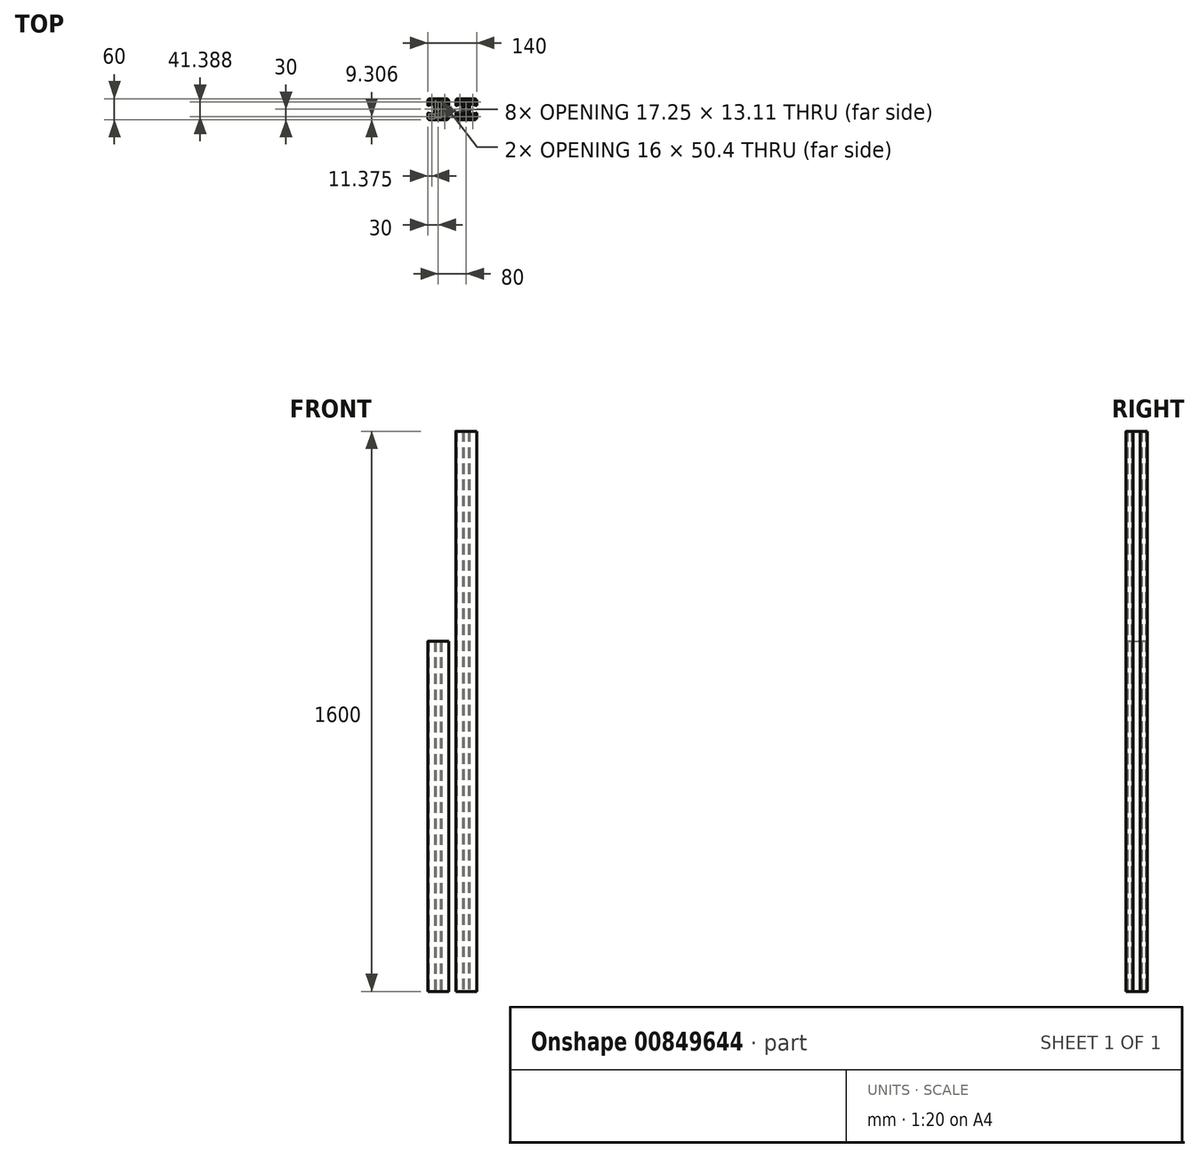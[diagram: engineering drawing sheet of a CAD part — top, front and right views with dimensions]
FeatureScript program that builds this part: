
annotation { "Feature Type Name" : "Feature", "Feature Type Description" : "" }
export const myFeature = defineFeature(function(context is Context, id is Id, definition is map)
    precondition{}
    {
        {
            var Q0;
            Q0=qCreatedBy(makeId("Top.planeOp"),FACE);
            var sketch = newSketch(context, id + "F0", { "sketchPlane" : qUnion([Q0])});
            skLineSegment(sketch, "E0", {"start": v(-5.2, -25.2) * mm, "end": v(5.2, -25.2) * mm});
            skLineSegment(sketch, "E1", {"start": v(6.2, -24.2) * mm, "end": v(6.2, -5.4) * mm});
            skLineSegment(sketch, "E2", {"start": v(6.2, 5.4) * mm, "end": v(6.2, 24.2) * mm});
            skLineSegment(sketch, "E3", {"start": v(5.2, 25.2) * mm, "end": v(-5.2, 25.2) * mm});
            skLineSegment(sketch, "E4", {"start": v(-6.2, 24.2) * mm, "end": v(-6.2, 5.4) * mm});
            skLineSegment(sketch, "E5", {"start": v(-6.2, -5.4) * mm, "end": v(-6.2, -24.2) * mm});
            skLineSegment(sketch, "E6", {"start": v(-24, -27.25) * mm, "end": v(-11, -27.25) * mm});
            skLineSegment(sketch, "E7", {"start": v(-10, -26.25) * mm, "end": v(-10, -19.22) * mm});
            skLineSegment(sketch, "E8", {"start": v(-10.74, -18.26) * mm, "end": v(-26, -14.17) * mm});
            skLineSegment(sketch, "E9", {"start": v(-27.25, -15.14) * mm, "end": v(-27.25, -24) * mm});
            skLineSegment(sketch, "E10", {"start": v(-26, 14.17) * mm, "end": v(-10.74, 18.26) * mm});
            skLineSegment(sketch, "E11", {"start": v(-10, 19.22) * mm, "end": v(-10, 26.25) * mm});
            skLineSegment(sketch, "E12", {"start": v(-11, 27.25) * mm, "end": v(-24, 27.25) * mm});
            skLineSegment(sketch, "E13", {"start": v(-27.25, 24) * mm, "end": v(-27.25, 15.14) * mm});
            skLineSegment(sketch, "E14", {"start": v(10, -14.3) * mm, "end": v(10, 14.3) * mm});
            skLineSegment(sketch, "E15", {"start": v(28.43, -10.67) * mm, "end": v(11.26, -15.27) * mm});
            skLineSegment(sketch, "E16", {"start": v(30, -24) * mm, "end": v(30, -11.88) * mm});
            skLineSegment(sketch, "E17", {"start": v(-24, -30) * mm, "end": v(24, -30) * mm});
            skLineSegment(sketch, "E18", {"start": v(-30, -11.88) * mm, "end": v(-30, -24) * mm});
            skLineSegment(sketch, "E19", {"start": v(-11.26, -15.27) * mm, "end": v(-28.43, -10.67) * mm});
            skLineSegment(sketch, "E20", {"start": v(-10, 14.3) * mm, "end": v(-10, -14.3) * mm});
            skLineSegment(sketch, "E21", {"start": v(-28.43, 10.67) * mm, "end": v(-11.26, 15.27) * mm});
            skLineSegment(sketch, "E22", {"start": v(-30, 24) * mm, "end": v(-30, 11.88) * mm});
            skLineSegment(sketch, "E23", {"start": v(24, 30) * mm, "end": v(-24, 30) * mm});
            skLineSegment(sketch, "E24", {"start": v(30, 11.88) * mm, "end": v(30, 24) * mm});
            skLineSegment(sketch, "E25", {"start": v(11.26, 15.27) * mm, "end": v(28.43, 10.67) * mm});
            skLineSegment(sketch, "E26", {"start": v(26, -14.17) * mm, "end": v(10.74, -18.26) * mm});
            skLineSegment(sketch, "E27", {"start": v(10, -19.22) * mm, "end": v(10, -26.25) * mm});
            skLineSegment(sketch, "E28", {"start": v(11, -27.25) * mm, "end": v(24, -27.25) * mm});
            skLineSegment(sketch, "E29", {"start": v(27.25, -24) * mm, "end": v(27.25, -15.14) * mm});
            skLineSegment(sketch, "E30", {"start": v(24, 27.25) * mm, "end": v(11, 27.25) * mm});
            skLineSegment(sketch, "E31", {"start": v(10, 26.25) * mm, "end": v(10, 19.22) * mm});
            skLineSegment(sketch, "E32", {"start": v(10.74, 18.26) * mm, "end": v(26, 14.17) * mm});
            skLineSegment(sketch, "E33", {"start": v(27.25, 15.14) * mm, "end": v(27.25, 24) * mm});
            skArc(sketch, "E34", {"start": v(-6.2, -24.2) * mm, "mid": v(-5.9, -24.9) * mm, "end": v(-5.2, -25.2) * mm});
            skArc(sketch, "E35", {"start": v(5.2, -25.2) * mm, "mid": v(5.9, -24.9) * mm, "end": v(6.2, -24.2) * mm});
            skArc(sketch, "E36", {"start": v(6.4, -4.8) * mm, "mid": v(6.25, -5.08) * mm, "end": v(6.2, -5.4) * mm});
            skArc(sketch, "E37", {"start": v(6.4, -4.8) * mm, "mid": v(8, 0) * mm, "end": v(6.4, 4.8) * mm});
            skArc(sketch, "E38", {"start": v(6.2, 5.4) * mm, "mid": v(6.25, 5.08) * mm, "end": v(6.4, 4.8) * mm});
            skArc(sketch, "E39", {"start": v(6.2, 24.2) * mm, "mid": v(5.9, 24.9) * mm, "end": v(5.2, 25.2) * mm});
            skArc(sketch, "E40", {"start": v(-5.2, 25.2) * mm, "mid": v(-5.9, 24.9) * mm, "end": v(-6.2, 24.2) * mm});
            skArc(sketch, "E41", {"start": v(-6.4, 4.8) * mm, "mid": v(-6.25, 5.08) * mm, "end": v(-6.2, 5.4) * mm});
            skArc(sketch, "E42", {"start": v(-6.4, 4.8) * mm, "mid": v(-8, 0) * mm, "end": v(-6.4, -4.8) * mm});
            skArc(sketch, "E43", {"start": v(-6.2, -5.4) * mm, "mid": v(-6.25, -5.08) * mm, "end": v(-6.4, -4.8) * mm});
            skArc(sketch, "E44", {"start": v(-27.25, -24) * mm, "mid": v(-26.3, -26.3) * mm, "end": v(-24, -27.25) * mm});
            skArc(sketch, "E45", {"start": v(-11, -27.25) * mm, "mid": v(-10.3, -26.96) * mm, "end": v(-10, -26.25) * mm});
            skArc(sketch, "E46", {"start": v(-10, -19.22) * mm, "mid": v(-10.2, -18.61) * mm, "end": v(-10.74, -18.26) * mm});
            skArc(sketch, "E47", {"start": v(-26, -14.17) * mm, "mid": v(-26.86, -14.34) * mm, "end": v(-27.25, -15.14) * mm});
            skArc(sketch, "E48", {"start": v(-27.25, 15.14) * mm, "mid": v(-26.86, 14.34) * mm, "end": v(-26, 14.17) * mm});
            skArc(sketch, "E49", {"start": v(-10.74, 18.26) * mm, "mid": v(-10.2, 18.61) * mm, "end": v(-10, 19.22) * mm});
            skArc(sketch, "E50", {"start": v(-10, 26.25) * mm, "mid": v(-10.3, 26.96) * mm, "end": v(-11, 27.25) * mm});
            skArc(sketch, "E51", {"start": v(-24, 27.25) * mm, "mid": v(-26.3, 26.3) * mm, "end": v(-27.25, 24) * mm});
            skArc(sketch, "E52", {"start": v(11.26, 15.27) * mm, "mid": v(10.4, 15.1) * mm, "end": v(10, 14.3) * mm});
            skArc(sketch, "E53", {"start": v(10, -14.3) * mm, "mid": v(10.4, -15.1) * mm, "end": v(11.26, -15.27) * mm});
            skArc(sketch, "E54", {"start": v(30, -11.88) * mm, "mid": v(29.51, -10.89) * mm, "end": v(28.43, -10.67) * mm});
            skArc(sketch, "E55", {"start": v(24, -30) * mm, "mid": v(28.24, -28.24) * mm, "end": v(30, -24) * mm});
            skArc(sketch, "E56", {"start": v(-30, -24) * mm, "mid": v(-28.24, -28.24) * mm, "end": v(-24, -30) * mm});
            skArc(sketch, "E57", {"start": v(-28.43, -10.67) * mm, "mid": v(-29.51, -10.89) * mm, "end": v(-30, -11.88) * mm});
            skArc(sketch, "E58", {"start": v(-11.26, -15.27) * mm, "mid": v(-10.4, -15.1) * mm, "end": v(-10, -14.3) * mm});
            skArc(sketch, "E59", {"start": v(-10, 14.3) * mm, "mid": v(-10.4, 15.1) * mm, "end": v(-11.26, 15.27) * mm});
            skArc(sketch, "E60", {"start": v(-30, 11.88) * mm, "mid": v(-29.51, 10.89) * mm, "end": v(-28.43, 10.67) * mm});
            skArc(sketch, "E61", {"start": v(-24, 30) * mm, "mid": v(-28.24, 28.24) * mm, "end": v(-30, 24) * mm});
            skArc(sketch, "E62", {"start": v(30, 24) * mm, "mid": v(28.24, 28.24) * mm, "end": v(24, 30) * mm});
            skArc(sketch, "E63", {"start": v(28.43, 10.67) * mm, "mid": v(29.51, 10.89) * mm, "end": v(30, 11.88) * mm});
            skArc(sketch, "E64", {"start": v(27.25, -15.14) * mm, "mid": v(26.86, -14.34) * mm, "end": v(26, -14.17) * mm});
            skArc(sketch, "E65", {"start": v(10.74, -18.26) * mm, "mid": v(10.2, -18.61) * mm, "end": v(10, -19.22) * mm});
            skArc(sketch, "E66", {"start": v(10, -26.25) * mm, "mid": v(10.3, -26.96) * mm, "end": v(11, -27.25) * mm});
            skArc(sketch, "E67", {"start": v(24, -27.25) * mm, "mid": v(26.3, -26.3) * mm, "end": v(27.25, -24) * mm});
            skArc(sketch, "E68", {"start": v(11, 27.25) * mm, "mid": v(10.3, 26.96) * mm, "end": v(10, 26.25) * mm});
            skArc(sketch, "E69", {"start": v(10, 19.22) * mm, "mid": v(10.2, 18.61) * mm, "end": v(10.74, 18.26) * mm});
            skArc(sketch, "E70", {"start": v(26, 14.17) * mm, "mid": v(26.86, 14.34) * mm, "end": v(27.25, 15.14) * mm});
            skArc(sketch, "E71", {"start": v(27.25, 24) * mm, "mid": v(26.3, 26.3) * mm, "end": v(24, 27.25) * mm});
            skLineSegment(sketch, "E72.1.0.0", {"start": v(90.74, 18.26) * mm, "end": v(106, 14.17) * mm});
            skLineSegment(sketch, "E72.1.0.1", {"start": v(56, -30) * mm, "end": v(104, -30) * mm});
            skLineSegment(sketch, "E72.1.0.2", {"start": v(108.43, -10.67) * mm, "end": v(91.26, -15.27) * mm});
            skLineSegment(sketch, "E72.1.0.3", {"start": v(107.25, 15.14) * mm, "end": v(107.25, 24) * mm});
            skLineSegment(sketch, "E72.1.0.4", {"start": v(86.2, 5.4) * mm, "end": v(86.2, 24.2) * mm});
            skLineSegment(sketch, "E72.1.0.5", {"start": v(91, -27.25) * mm, "end": v(104, -27.25) * mm});
            skLineSegment(sketch, "E72.1.0.6", {"start": v(86.2, -24.2) * mm, "end": v(86.2, -5.4) * mm});
            skLineSegment(sketch, "E72.1.0.7", {"start": v(51.57, 10.67) * mm, "end": v(68.74, 15.27) * mm});
            skLineSegment(sketch, "E72.1.0.8", {"start": v(50, -11.88) * mm, "end": v(50, -24) * mm});
            skLineSegment(sketch, "E72.1.0.9", {"start": v(74.8, -25.2) * mm, "end": v(85.2, -25.2) * mm});
            skLineSegment(sketch, "E72.1.0.10", {"start": v(70, 14.3) * mm, "end": v(70, -14.3) * mm});
            skLineSegment(sketch, "E72.1.0.11", {"start": v(90, -14.3) * mm, "end": v(90, 14.3) * mm});
            skLineSegment(sketch, "E72.1.0.12", {"start": v(73.8, -5.4) * mm, "end": v(73.8, -24.2) * mm});
            skArc(sketch, "E72.1.0.13", {"start": v(56, 30) * mm, "mid": v(51.76, 28.24) * mm, "end": v(50, 24) * mm});
            skLineSegment(sketch, "E72.1.0.14", {"start": v(69.26, -18.26) * mm, "end": v(54, -14.17) * mm});
            skArc(sketch, "E72.1.0.15", {"start": v(110, 24) * mm, "mid": v(108.24, 28.24) * mm, "end": v(104, 30) * mm});
            skArc(sketch, "E72.1.0.16", {"start": v(104, -30) * mm, "mid": v(108.24, -28.24) * mm, "end": v(110, -24) * mm});
            skLineSegment(sketch, "E72.1.0.17", {"start": v(73.8, 24.2) * mm, "end": v(73.8, 5.4) * mm});
            skLineSegment(sketch, "E72.1.0.18", {"start": v(104, 30) * mm, "end": v(56, 30) * mm});
            skLineSegment(sketch, "E72.1.0.19", {"start": v(56, -27.25) * mm, "end": v(69, -27.25) * mm});
            skLineSegment(sketch, "E72.1.0.20", {"start": v(54, 14.17) * mm, "end": v(69.26, 18.26) * mm});
            skLineSegment(sketch, "E72.1.0.21", {"start": v(50, 24) * mm, "end": v(50, 11.88) * mm});
            skLineSegment(sketch, "E72.1.0.22", {"start": v(85.2, 25.2) * mm, "end": v(74.8, 25.2) * mm});
            skLineSegment(sketch, "E72.1.0.23", {"start": v(91.26, 15.27) * mm, "end": v(108.43, 10.67) * mm});
            skLineSegment(sketch, "E72.1.0.24", {"start": v(52.75, 24) * mm, "end": v(52.75, 15.14) * mm});
            skLineSegment(sketch, "E72.1.0.25", {"start": v(107.25, -24) * mm, "end": v(107.25, -15.14) * mm});
            skArc(sketch, "E72.1.0.26", {"start": v(73.6, 4.8) * mm, "mid": v(72, 0) * mm, "end": v(73.6, -4.8) * mm});
            skLineSegment(sketch, "E72.1.0.27", {"start": v(52.75, -15.14) * mm, "end": v(52.75, -24) * mm});
            skLineSegment(sketch, "E72.1.0.28", {"start": v(106, -14.17) * mm, "end": v(90.74, -18.26) * mm});
            skLineSegment(sketch, "E72.1.0.29", {"start": v(68.74, -15.27) * mm, "end": v(51.57, -10.67) * mm});
            skLineSegment(sketch, "E72.1.0.30", {"start": v(110, 11.88) * mm, "end": v(110, 24) * mm});
            skLineSegment(sketch, "E72.1.0.31", {"start": v(104, 27.25) * mm, "end": v(91, 27.25) * mm});
            skArc(sketch, "E72.1.0.32", {"start": v(86.4, -4.8) * mm, "mid": v(88, 0) * mm, "end": v(86.4, 4.8) * mm});
            skArc(sketch, "E72.1.0.33", {"start": v(50, -24) * mm, "mid": v(51.76, -28.24) * mm, "end": v(56, -30) * mm});
            skLineSegment(sketch, "E72.1.0.34", {"start": v(110, -24) * mm, "end": v(110, -11.88) * mm});
            skLineSegment(sketch, "E72.1.0.35", {"start": v(69, 27.25) * mm, "end": v(56, 27.25) * mm});
            skArc(sketch, "E72.1.0.36", {"start": v(85.2, -25.2) * mm, "mid": v(85.9, -24.9) * mm, "end": v(86.2, -24.2) * mm});
            skArc(sketch, "E72.1.0.37", {"start": v(52.75, -24) * mm, "mid": v(53.7, -26.3) * mm, "end": v(56, -27.25) * mm});
            skArc(sketch, "E72.1.0.38", {"start": v(107.25, -15.14) * mm, "mid": v(106.86, -14.34) * mm, "end": v(106, -14.17) * mm});
            skArc(sketch, "E72.1.0.39", {"start": v(90, -26.25) * mm, "mid": v(90.3, -26.96) * mm, "end": v(91, -27.25) * mm});
            skArc(sketch, "E72.1.0.40", {"start": v(86.2, 5.4) * mm, "mid": v(86.25, 5.08) * mm, "end": v(86.4, 4.8) * mm});
            skArc(sketch, "E72.1.0.41", {"start": v(104, -27.25) * mm, "mid": v(106.3, -26.3) * mm, "end": v(107.25, -24) * mm});
            skArc(sketch, "E72.1.0.42", {"start": v(73.6, 4.8) * mm, "mid": v(73.75, 5.08) * mm, "end": v(73.8, 5.4) * mm});
            skLineSegment(sketch, "E72.1.0.43", {"start": v(90, 26.25) * mm, "end": v(90, 19.22) * mm});
            skArc(sketch, "E72.1.0.44", {"start": v(110, -11.88) * mm, "mid": v(109.51, -10.89) * mm, "end": v(108.43, -10.67) * mm});
            skArc(sketch, "E72.1.0.45", {"start": v(90, -14.3) * mm, "mid": v(90.4, -15.1) * mm, "end": v(91.26, -15.27) * mm});
            skArc(sketch, "E72.1.0.46", {"start": v(91, 27.25) * mm, "mid": v(90.3, 26.96) * mm, "end": v(90, 26.25) * mm});
            skArc(sketch, "E72.1.0.47", {"start": v(56, 27.25) * mm, "mid": v(53.7, 26.3) * mm, "end": v(52.75, 24) * mm});
            skArc(sketch, "E72.1.0.48", {"start": v(106, 14.17) * mm, "mid": v(106.86, 14.34) * mm, "end": v(107.25, 15.14) * mm});
            skArc(sketch, "E72.1.0.49", {"start": v(108.43, 10.67) * mm, "mid": v(109.51, 10.89) * mm, "end": v(110, 11.88) * mm});
            skArc(sketch, "E72.1.0.50", {"start": v(90, 19.22) * mm, "mid": v(90.2, 18.61) * mm, "end": v(90.74, 18.26) * mm});
            skArc(sketch, "E72.1.0.51", {"start": v(91.26, 15.27) * mm, "mid": v(90.4, 15.1) * mm, "end": v(90, 14.3) * mm});
            skArc(sketch, "E72.1.0.52", {"start": v(107.25, 24) * mm, "mid": v(106.3, 26.3) * mm, "end": v(104, 27.25) * mm});
            skArc(sketch, "E72.1.0.53", {"start": v(51.57, -10.67) * mm, "mid": v(50.49, -10.89) * mm, "end": v(50, -11.88) * mm});
            skLineSegment(sketch, "E72.1.0.54", {"start": v(90, -19.22) * mm, "end": v(90, -26.25) * mm});
            skArc(sketch, "E72.1.0.55", {"start": v(73.8, -24.2) * mm, "mid": v(74.1, -24.9) * mm, "end": v(74.8, -25.2) * mm});
            skArc(sketch, "E72.1.0.56", {"start": v(90.74, -18.26) * mm, "mid": v(90.2, -18.61) * mm, "end": v(90, -19.22) * mm});
            skArc(sketch, "E72.1.0.57", {"start": v(54, -14.17) * mm, "mid": v(53.14, -14.34) * mm, "end": v(52.75, -15.14) * mm});
            skArc(sketch, "E72.1.0.58", {"start": v(50, 11.88) * mm, "mid": v(50.49, 10.89) * mm, "end": v(51.57, 10.67) * mm});
            skLineSegment(sketch, "E72.1.0.59", {"start": v(70, -26.25) * mm, "end": v(70, -19.22) * mm});
            skArc(sketch, "E72.1.0.60", {"start": v(69.26, 18.26) * mm, "mid": v(69.8, 18.61) * mm, "end": v(70, 19.22) * mm});
            skArc(sketch, "E72.1.0.61", {"start": v(86.2, 24.2) * mm, "mid": v(85.9, 24.9) * mm, "end": v(85.2, 25.2) * mm});
            skArc(sketch, "E72.1.0.62", {"start": v(52.75, 15.14) * mm, "mid": v(53.14, 14.34) * mm, "end": v(54, 14.17) * mm});
            skArc(sketch, "E72.1.0.63", {"start": v(70, -19.22) * mm, "mid": v(69.8, -18.61) * mm, "end": v(69.26, -18.26) * mm});
            skArc(sketch, "E72.1.0.64", {"start": v(74.8, 25.2) * mm, "mid": v(74.1, 24.9) * mm, "end": v(73.8, 24.2) * mm});
            skArc(sketch, "E72.1.0.65", {"start": v(70, 26.25) * mm, "mid": v(69.7, 26.96) * mm, "end": v(69, 27.25) * mm});
            skArc(sketch, "E72.1.0.66", {"start": v(70, 14.3) * mm, "mid": v(69.6, 15.1) * mm, "end": v(68.74, 15.27) * mm});
            skLineSegment(sketch, "E72.1.0.67", {"start": v(70, 19.22) * mm, "end": v(70, 26.25) * mm});
            skArc(sketch, "E72.1.0.68", {"start": v(68.74, -15.27) * mm, "mid": v(69.6, -15.1) * mm, "end": v(70, -14.3) * mm});
            skArc(sketch, "E72.1.0.69", {"start": v(69, -27.25) * mm, "mid": v(69.7, -26.96) * mm, "end": v(70, -26.25) * mm});
            skArc(sketch, "E72.1.0.70", {"start": v(86.4, -4.8) * mm, "mid": v(86.25, -5.08) * mm, "end": v(86.2, -5.4) * mm});
            skArc(sketch, "E72.1.0.71", {"start": v(73.8, -5.4) * mm, "mid": v(73.75, -5.08) * mm, "end": v(73.6, -4.8) * mm});
            skLineSegment(sketch, "E72.2.0.0", {"start": v(170.74, 18.26) * mm, "end": v(186, 14.17) * mm});
            skLineSegment(sketch, "E72.2.0.1", {"start": v(136, -30) * mm, "end": v(184, -30) * mm});
            skLineSegment(sketch, "E72.2.0.2", {"start": v(188.43, -10.67) * mm, "end": v(171.26, -15.27) * mm});
            skLineSegment(sketch, "E72.2.0.3", {"start": v(187.25, 15.14) * mm, "end": v(187.25, 24) * mm});
            skLineSegment(sketch, "E72.2.0.4", {"start": v(166.2, 5.4) * mm, "end": v(166.2, 24.2) * mm});
            skLineSegment(sketch, "E72.2.0.5", {"start": v(171, -27.25) * mm, "end": v(184, -27.25) * mm});
            skLineSegment(sketch, "E72.2.0.6", {"start": v(166.2, -24.2) * mm, "end": v(166.2, -5.4) * mm});
            skLineSegment(sketch, "E72.2.0.7", {"start": v(131.57, 10.67) * mm, "end": v(148.74, 15.27) * mm});
            skLineSegment(sketch, "E72.2.0.8", {"start": v(130, -11.88) * mm, "end": v(130, -24) * mm});
            skLineSegment(sketch, "E72.2.0.9", {"start": v(154.8, -25.2) * mm, "end": v(165.2, -25.2) * mm});
            skLineSegment(sketch, "E72.2.0.10", {"start": v(150, 14.3) * mm, "end": v(150, -14.3) * mm});
            skLineSegment(sketch, "E72.2.0.11", {"start": v(170, -14.3) * mm, "end": v(170, 14.3) * mm});
            skLineSegment(sketch, "E72.2.0.12", {"start": v(153.8, -5.4) * mm, "end": v(153.8, -24.2) * mm});
            skArc(sketch, "E72.2.0.13", {"start": v(136, 30) * mm, "mid": v(131.76, 28.24) * mm, "end": v(130, 24) * mm});
            skLineSegment(sketch, "E72.2.0.14", {"start": v(149.26, -18.26) * mm, "end": v(134, -14.17) * mm});
            skArc(sketch, "E72.2.0.15", {"start": v(190, 24) * mm, "mid": v(188.24, 28.24) * mm, "end": v(184, 30) * mm});
            skArc(sketch, "E72.2.0.16", {"start": v(184, -30) * mm, "mid": v(188.24, -28.24) * mm, "end": v(190, -24) * mm});
            skLineSegment(sketch, "E72.2.0.17", {"start": v(153.8, 24.2) * mm, "end": v(153.8, 5.4) * mm});
            skLineSegment(sketch, "E72.2.0.18", {"start": v(184, 30) * mm, "end": v(136, 30) * mm});
            skLineSegment(sketch, "E72.2.0.19", {"start": v(136, -27.25) * mm, "end": v(149, -27.25) * mm});
            skLineSegment(sketch, "E72.2.0.20", {"start": v(134, 14.17) * mm, "end": v(149.26, 18.26) * mm});
            skLineSegment(sketch, "E72.2.0.21", {"start": v(130, 24) * mm, "end": v(130, 11.88) * mm});
            skLineSegment(sketch, "E72.2.0.22", {"start": v(165.2, 25.2) * mm, "end": v(154.8, 25.2) * mm});
            skLineSegment(sketch, "E72.2.0.23", {"start": v(171.26, 15.27) * mm, "end": v(188.43, 10.67) * mm});
            skLineSegment(sketch, "E72.2.0.24", {"start": v(132.75, 24) * mm, "end": v(132.75, 15.14) * mm});
            skLineSegment(sketch, "E72.2.0.25", {"start": v(187.25, -24) * mm, "end": v(187.25, -15.14) * mm});
            skArc(sketch, "E72.2.0.26", {"start": v(153.6, 4.8) * mm, "mid": v(152, 0) * mm, "end": v(153.6, -4.8) * mm});
            skLineSegment(sketch, "E72.2.0.27", {"start": v(132.75, -15.14) * mm, "end": v(132.75, -24) * mm});
            skLineSegment(sketch, "E72.2.0.28", {"start": v(186, -14.17) * mm, "end": v(170.74, -18.26) * mm});
            skLineSegment(sketch, "E72.2.0.29", {"start": v(148.74, -15.27) * mm, "end": v(131.57, -10.67) * mm});
            skLineSegment(sketch, "E72.2.0.30", {"start": v(190, 11.88) * mm, "end": v(190, 24) * mm});
            skLineSegment(sketch, "E72.2.0.31", {"start": v(184, 27.25) * mm, "end": v(171, 27.25) * mm});
            skArc(sketch, "E72.2.0.32", {"start": v(166.4, -4.8) * mm, "mid": v(168, 0) * mm, "end": v(166.4, 4.8) * mm});
            skArc(sketch, "E72.2.0.33", {"start": v(130, -24) * mm, "mid": v(131.76, -28.24) * mm, "end": v(136, -30) * mm});
            skLineSegment(sketch, "E72.2.0.34", {"start": v(190, -24) * mm, "end": v(190, -11.88) * mm});
            skLineSegment(sketch, "E72.2.0.35", {"start": v(149, 27.25) * mm, "end": v(136, 27.25) * mm});
            skArc(sketch, "E72.2.0.36", {"start": v(165.2, -25.2) * mm, "mid": v(165.9, -24.9) * mm, "end": v(166.2, -24.2) * mm});
            skArc(sketch, "E72.2.0.37", {"start": v(132.75, -24) * mm, "mid": v(133.7, -26.3) * mm, "end": v(136, -27.25) * mm});
            skArc(sketch, "E72.2.0.38", {"start": v(187.25, -15.14) * mm, "mid": v(186.86, -14.34) * mm, "end": v(186, -14.17) * mm});
            skArc(sketch, "E72.2.0.39", {"start": v(170, -26.25) * mm, "mid": v(170.3, -26.96) * mm, "end": v(171, -27.25) * mm});
            skArc(sketch, "E72.2.0.40", {"start": v(166.2, 5.4) * mm, "mid": v(166.25, 5.08) * mm, "end": v(166.4, 4.8) * mm});
            skArc(sketch, "E72.2.0.41", {"start": v(184, -27.25) * mm, "mid": v(186.3, -26.3) * mm, "end": v(187.25, -24) * mm});
            skArc(sketch, "E72.2.0.42", {"start": v(153.6, 4.8) * mm, "mid": v(153.75, 5.08) * mm, "end": v(153.8, 5.4) * mm});
            skLineSegment(sketch, "E72.2.0.43", {"start": v(170, 26.25) * mm, "end": v(170, 19.22) * mm});
            skArc(sketch, "E72.2.0.44", {"start": v(190, -11.88) * mm, "mid": v(189.51, -10.89) * mm, "end": v(188.43, -10.67) * mm});
            skArc(sketch, "E72.2.0.45", {"start": v(170, -14.3) * mm, "mid": v(170.4, -15.1) * mm, "end": v(171.26, -15.27) * mm});
            skArc(sketch, "E72.2.0.46", {"start": v(171, 27.25) * mm, "mid": v(170.3, 26.96) * mm, "end": v(170, 26.25) * mm});
            skArc(sketch, "E72.2.0.47", {"start": v(136, 27.25) * mm, "mid": v(133.7, 26.3) * mm, "end": v(132.75, 24) * mm});
            skArc(sketch, "E72.2.0.48", {"start": v(186, 14.17) * mm, "mid": v(186.86, 14.34) * mm, "end": v(187.25, 15.14) * mm});
            skArc(sketch, "E72.2.0.49", {"start": v(188.43, 10.67) * mm, "mid": v(189.51, 10.89) * mm, "end": v(190, 11.88) * mm});
            skArc(sketch, "E72.2.0.50", {"start": v(170, 19.22) * mm, "mid": v(170.2, 18.61) * mm, "end": v(170.74, 18.26) * mm});
            skArc(sketch, "E72.2.0.51", {"start": v(171.26, 15.27) * mm, "mid": v(170.4, 15.1) * mm, "end": v(170, 14.3) * mm});
            skArc(sketch, "E72.2.0.52", {"start": v(187.25, 24) * mm, "mid": v(186.3, 26.3) * mm, "end": v(184, 27.25) * mm});
            skArc(sketch, "E72.2.0.53", {"start": v(131.57, -10.67) * mm, "mid": v(130.49, -10.89) * mm, "end": v(130, -11.88) * mm});
            skLineSegment(sketch, "E72.2.0.54", {"start": v(170, -19.22) * mm, "end": v(170, -26.25) * mm});
            skArc(sketch, "E72.2.0.55", {"start": v(153.8, -24.2) * mm, "mid": v(154.1, -24.9) * mm, "end": v(154.8, -25.2) * mm});
            skArc(sketch, "E72.2.0.56", {"start": v(170.74, -18.26) * mm, "mid": v(170.2, -18.61) * mm, "end": v(170, -19.22) * mm});
            skArc(sketch, "E72.2.0.57", {"start": v(134, -14.17) * mm, "mid": v(133.14, -14.34) * mm, "end": v(132.75, -15.14) * mm});
            skArc(sketch, "E72.2.0.58", {"start": v(130, 11.88) * mm, "mid": v(130.49, 10.89) * mm, "end": v(131.57, 10.67) * mm});
            skLineSegment(sketch, "E72.2.0.59", {"start": v(150, -26.25) * mm, "end": v(150, -19.22) * mm});
            skArc(sketch, "E72.2.0.60", {"start": v(149.26, 18.26) * mm, "mid": v(149.8, 18.61) * mm, "end": v(150, 19.22) * mm});
            skArc(sketch, "E72.2.0.61", {"start": v(166.2, 24.2) * mm, "mid": v(165.9, 24.9) * mm, "end": v(165.2, 25.2) * mm});
            skArc(sketch, "E72.2.0.62", {"start": v(132.75, 15.14) * mm, "mid": v(133.14, 14.34) * mm, "end": v(134, 14.17) * mm});
            skArc(sketch, "E72.2.0.63", {"start": v(150, -19.22) * mm, "mid": v(149.8, -18.61) * mm, "end": v(149.26, -18.26) * mm});
            skArc(sketch, "E72.2.0.64", {"start": v(154.8, 25.2) * mm, "mid": v(154.1, 24.9) * mm, "end": v(153.8, 24.2) * mm});
            skArc(sketch, "E72.2.0.65", {"start": v(150, 26.25) * mm, "mid": v(149.7, 26.96) * mm, "end": v(149, 27.25) * mm});
            skArc(sketch, "E72.2.0.66", {"start": v(150, 14.3) * mm, "mid": v(149.6, 15.1) * mm, "end": v(148.74, 15.27) * mm});
            skLineSegment(sketch, "E72.2.0.67", {"start": v(150, 19.22) * mm, "end": v(150, 26.25) * mm});
            skArc(sketch, "E72.2.0.68", {"start": v(148.74, -15.27) * mm, "mid": v(149.6, -15.1) * mm, "end": v(150, -14.3) * mm});
            skArc(sketch, "E72.2.0.69", {"start": v(149, -27.25) * mm, "mid": v(149.7, -26.96) * mm, "end": v(150, -26.25) * mm});
            skArc(sketch, "E72.2.0.70", {"start": v(166.4, -4.8) * mm, "mid": v(166.25, -5.08) * mm, "end": v(166.2, -5.4) * mm});
            skArc(sketch, "E72.2.0.71", {"start": v(153.8, -5.4) * mm, "mid": v(153.75, -5.08) * mm, "end": v(153.6, -4.8) * mm});
            skLineSegment(sketch, "E72.3.0.0", {"start": v(250.74, 18.26) * mm, "end": v(266, 14.17) * mm});
            skLineSegment(sketch, "E72.3.0.1", {"start": v(216, -30) * mm, "end": v(264, -30) * mm});
            skLineSegment(sketch, "E72.3.0.2", {"start": v(268.43, -10.67) * mm, "end": v(251.26, -15.27) * mm});
            skLineSegment(sketch, "E72.3.0.3", {"start": v(267.25, 15.14) * mm, "end": v(267.25, 24) * mm});
            skLineSegment(sketch, "E72.3.0.4", {"start": v(246.2, 5.4) * mm, "end": v(246.2, 24.2) * mm});
            skLineSegment(sketch, "E72.3.0.5", {"start": v(251, -27.25) * mm, "end": v(264, -27.25) * mm});
            skLineSegment(sketch, "E72.3.0.6", {"start": v(246.2, -24.2) * mm, "end": v(246.2, -5.4) * mm});
            skLineSegment(sketch, "E72.3.0.7", {"start": v(211.57, 10.67) * mm, "end": v(228.74, 15.27) * mm});
            skLineSegment(sketch, "E72.3.0.8", {"start": v(210, -11.88) * mm, "end": v(210, -24) * mm});
            skLineSegment(sketch, "E72.3.0.9", {"start": v(234.8, -25.2) * mm, "end": v(245.2, -25.2) * mm});
            skLineSegment(sketch, "E72.3.0.10", {"start": v(230, 14.3) * mm, "end": v(230, -14.3) * mm});
            skLineSegment(sketch, "E72.3.0.11", {"start": v(250, -14.3) * mm, "end": v(250, 14.3) * mm});
            skLineSegment(sketch, "E72.3.0.12", {"start": v(233.8, -5.4) * mm, "end": v(233.8, -24.2) * mm});
            skArc(sketch, "E72.3.0.13", {"start": v(216, 30) * mm, "mid": v(211.76, 28.24) * mm, "end": v(210, 24) * mm});
            skLineSegment(sketch, "E72.3.0.14", {"start": v(229.26, -18.26) * mm, "end": v(214, -14.17) * mm});
            skArc(sketch, "E72.3.0.15", {"start": v(270, 24) * mm, "mid": v(268.24, 28.24) * mm, "end": v(264, 30) * mm});
            skArc(sketch, "E72.3.0.16", {"start": v(264, -30) * mm, "mid": v(268.24, -28.24) * mm, "end": v(270, -24) * mm});
            skLineSegment(sketch, "E72.3.0.17", {"start": v(233.8, 24.2) * mm, "end": v(233.8, 5.4) * mm});
            skLineSegment(sketch, "E72.3.0.18", {"start": v(264, 30) * mm, "end": v(216, 30) * mm});
            skLineSegment(sketch, "E72.3.0.19", {"start": v(216, -27.25) * mm, "end": v(229, -27.25) * mm});
            skLineSegment(sketch, "E72.3.0.20", {"start": v(214, 14.17) * mm, "end": v(229.26, 18.26) * mm});
            skLineSegment(sketch, "E72.3.0.21", {"start": v(210, 24) * mm, "end": v(210, 11.88) * mm});
            skLineSegment(sketch, "E72.3.0.22", {"start": v(245.2, 25.2) * mm, "end": v(234.8, 25.2) * mm});
            skLineSegment(sketch, "E72.3.0.23", {"start": v(251.26, 15.27) * mm, "end": v(268.43, 10.67) * mm});
            skLineSegment(sketch, "E72.3.0.24", {"start": v(212.75, 24) * mm, "end": v(212.75, 15.14) * mm});
            skLineSegment(sketch, "E72.3.0.25", {"start": v(267.25, -24) * mm, "end": v(267.25, -15.14) * mm});
            skArc(sketch, "E72.3.0.26", {"start": v(233.6, 4.8) * mm, "mid": v(232, 0) * mm, "end": v(233.6, -4.8) * mm});
            skLineSegment(sketch, "E72.3.0.27", {"start": v(212.75, -15.14) * mm, "end": v(212.75, -24) * mm});
            skLineSegment(sketch, "E72.3.0.28", {"start": v(266, -14.17) * mm, "end": v(250.74, -18.26) * mm});
            skLineSegment(sketch, "E72.3.0.29", {"start": v(228.74, -15.27) * mm, "end": v(211.57, -10.67) * mm});
            skLineSegment(sketch, "E72.3.0.30", {"start": v(270, 11.88) * mm, "end": v(270, 24) * mm});
            skLineSegment(sketch, "E72.3.0.31", {"start": v(264, 27.25) * mm, "end": v(251, 27.25) * mm});
            skArc(sketch, "E72.3.0.32", {"start": v(246.4, -4.8) * mm, "mid": v(248, 0) * mm, "end": v(246.4, 4.8) * mm});
            skArc(sketch, "E72.3.0.33", {"start": v(210, -24) * mm, "mid": v(211.76, -28.24) * mm, "end": v(216, -30) * mm});
            skLineSegment(sketch, "E72.3.0.34", {"start": v(270, -24) * mm, "end": v(270, -11.88) * mm});
            skLineSegment(sketch, "E72.3.0.35", {"start": v(229, 27.25) * mm, "end": v(216, 27.25) * mm});
            skArc(sketch, "E72.3.0.36", {"start": v(245.2, -25.2) * mm, "mid": v(245.9, -24.9) * mm, "end": v(246.2, -24.2) * mm});
            skArc(sketch, "E72.3.0.37", {"start": v(212.75, -24) * mm, "mid": v(213.7, -26.3) * mm, "end": v(216, -27.25) * mm});
            skArc(sketch, "E72.3.0.38", {"start": v(267.25, -15.14) * mm, "mid": v(266.86, -14.34) * mm, "end": v(266, -14.17) * mm});
            skArc(sketch, "E72.3.0.39", {"start": v(250, -26.25) * mm, "mid": v(250.3, -26.96) * mm, "end": v(251, -27.25) * mm});
            skArc(sketch, "E72.3.0.40", {"start": v(246.2, 5.4) * mm, "mid": v(246.25, 5.08) * mm, "end": v(246.4, 4.8) * mm});
            skArc(sketch, "E72.3.0.41", {"start": v(264, -27.25) * mm, "mid": v(266.3, -26.3) * mm, "end": v(267.25, -24) * mm});
            skArc(sketch, "E72.3.0.42", {"start": v(233.6, 4.8) * mm, "mid": v(233.75, 5.08) * mm, "end": v(233.8, 5.4) * mm});
            skLineSegment(sketch, "E72.3.0.43", {"start": v(250, 26.25) * mm, "end": v(250, 19.22) * mm});
            skArc(sketch, "E72.3.0.44", {"start": v(270, -11.88) * mm, "mid": v(269.51, -10.89) * mm, "end": v(268.43, -10.67) * mm});
            skArc(sketch, "E72.3.0.45", {"start": v(250, -14.3) * mm, "mid": v(250.4, -15.1) * mm, "end": v(251.26, -15.27) * mm});
            skArc(sketch, "E72.3.0.46", {"start": v(251, 27.25) * mm, "mid": v(250.3, 26.96) * mm, "end": v(250, 26.25) * mm});
            skArc(sketch, "E72.3.0.47", {"start": v(216, 27.25) * mm, "mid": v(213.7, 26.3) * mm, "end": v(212.75, 24) * mm});
            skArc(sketch, "E72.3.0.48", {"start": v(266, 14.17) * mm, "mid": v(266.86, 14.34) * mm, "end": v(267.25, 15.14) * mm});
            skArc(sketch, "E72.3.0.49", {"start": v(268.43, 10.67) * mm, "mid": v(269.51, 10.89) * mm, "end": v(270, 11.88) * mm});
            skArc(sketch, "E72.3.0.50", {"start": v(250, 19.22) * mm, "mid": v(250.2, 18.61) * mm, "end": v(250.74, 18.26) * mm});
            skArc(sketch, "E72.3.0.51", {"start": v(251.26, 15.27) * mm, "mid": v(250.4, 15.1) * mm, "end": v(250, 14.3) * mm});
            skArc(sketch, "E72.3.0.52", {"start": v(267.25, 24) * mm, "mid": v(266.3, 26.3) * mm, "end": v(264, 27.25) * mm});
            skArc(sketch, "E72.3.0.53", {"start": v(211.57, -10.67) * mm, "mid": v(210.49, -10.89) * mm, "end": v(210, -11.88) * mm});
            skLineSegment(sketch, "E72.3.0.54", {"start": v(250, -19.22) * mm, "end": v(250, -26.25) * mm});
            skArc(sketch, "E72.3.0.55", {"start": v(233.8, -24.2) * mm, "mid": v(234.1, -24.9) * mm, "end": v(234.8, -25.2) * mm});
            skArc(sketch, "E72.3.0.56", {"start": v(250.74, -18.26) * mm, "mid": v(250.2, -18.61) * mm, "end": v(250, -19.22) * mm});
            skArc(sketch, "E72.3.0.57", {"start": v(214, -14.17) * mm, "mid": v(213.14, -14.34) * mm, "end": v(212.75, -15.14) * mm});
            skArc(sketch, "E72.3.0.58", {"start": v(210, 11.88) * mm, "mid": v(210.49, 10.89) * mm, "end": v(211.57, 10.67) * mm});
            skLineSegment(sketch, "E72.3.0.59", {"start": v(230, -26.25) * mm, "end": v(230, -19.22) * mm});
            skArc(sketch, "E72.3.0.60", {"start": v(229.26, 18.26) * mm, "mid": v(229.8, 18.61) * mm, "end": v(230, 19.22) * mm});
            skArc(sketch, "E72.3.0.61", {"start": v(246.2, 24.2) * mm, "mid": v(245.9, 24.9) * mm, "end": v(245.2, 25.2) * mm});
            skArc(sketch, "E72.3.0.62", {"start": v(212.75, 15.14) * mm, "mid": v(213.14, 14.34) * mm, "end": v(214, 14.17) * mm});
            skArc(sketch, "E72.3.0.63", {"start": v(230, -19.22) * mm, "mid": v(229.8, -18.61) * mm, "end": v(229.26, -18.26) * mm});
            skArc(sketch, "E72.3.0.64", {"start": v(234.8, 25.2) * mm, "mid": v(234.1, 24.9) * mm, "end": v(233.8, 24.2) * mm});
            skArc(sketch, "E72.3.0.65", {"start": v(230, 26.25) * mm, "mid": v(229.7, 26.96) * mm, "end": v(229, 27.25) * mm});
            skArc(sketch, "E72.3.0.66", {"start": v(230, 14.3) * mm, "mid": v(229.6, 15.1) * mm, "end": v(228.74, 15.27) * mm});
            skLineSegment(sketch, "E72.3.0.67", {"start": v(230, 19.22) * mm, "end": v(230, 26.25) * mm});
            skArc(sketch, "E72.3.0.68", {"start": v(228.74, -15.27) * mm, "mid": v(229.6, -15.1) * mm, "end": v(230, -14.3) * mm});
            skArc(sketch, "E72.3.0.69", {"start": v(229, -27.25) * mm, "mid": v(229.7, -26.96) * mm, "end": v(230, -26.25) * mm});
            skArc(sketch, "E72.3.0.70", {"start": v(246.4, -4.8) * mm, "mid": v(246.25, -5.08) * mm, "end": v(246.2, -5.4) * mm});
            skArc(sketch, "E72.3.0.71", {"start": v(233.8, -5.4) * mm, "mid": v(233.75, -5.08) * mm, "end": v(233.6, -4.8) * mm});
            skLineSegment(sketch, "E72.4.0.0", {"start": v(330.74, 18.26) * mm, "end": v(346, 14.17) * mm});
            skLineSegment(sketch, "E72.4.0.1", {"start": v(296, -30) * mm, "end": v(344, -30) * mm});
            skLineSegment(sketch, "E72.4.0.2", {"start": v(348.43, -10.67) * mm, "end": v(331.26, -15.27) * mm});
            skLineSegment(sketch, "E72.4.0.3", {"start": v(347.25, 15.14) * mm, "end": v(347.25, 24) * mm});
            skLineSegment(sketch, "E72.4.0.4", {"start": v(326.2, 5.4) * mm, "end": v(326.2, 24.2) * mm});
            skLineSegment(sketch, "E72.4.0.5", {"start": v(331, -27.25) * mm, "end": v(344, -27.25) * mm});
            skLineSegment(sketch, "E72.4.0.6", {"start": v(326.2, -24.2) * mm, "end": v(326.2, -5.4) * mm});
            skLineSegment(sketch, "E72.4.0.7", {"start": v(291.57, 10.67) * mm, "end": v(308.74, 15.27) * mm});
            skLineSegment(sketch, "E72.4.0.8", {"start": v(290, -11.88) * mm, "end": v(290, -24) * mm});
            skLineSegment(sketch, "E72.4.0.9", {"start": v(314.8, -25.2) * mm, "end": v(325.2, -25.2) * mm});
            skLineSegment(sketch, "E72.4.0.10", {"start": v(310, 14.3) * mm, "end": v(310, -14.3) * mm});
            skLineSegment(sketch, "E72.4.0.11", {"start": v(330, -14.3) * mm, "end": v(330, 14.3) * mm});
            skLineSegment(sketch, "E72.4.0.12", {"start": v(313.8, -5.4) * mm, "end": v(313.8, -24.2) * mm});
            skArc(sketch, "E72.4.0.13", {"start": v(296, 30) * mm, "mid": v(291.76, 28.24) * mm, "end": v(290, 24) * mm});
            skLineSegment(sketch, "E72.4.0.14", {"start": v(309.26, -18.26) * mm, "end": v(294, -14.17) * mm});
            skArc(sketch, "E72.4.0.15", {"start": v(350, 24) * mm, "mid": v(348.24, 28.24) * mm, "end": v(344, 30) * mm});
            skArc(sketch, "E72.4.0.16", {"start": v(344, -30) * mm, "mid": v(348.24, -28.24) * mm, "end": v(350, -24) * mm});
            skLineSegment(sketch, "E72.4.0.17", {"start": v(313.8, 24.2) * mm, "end": v(313.8, 5.4) * mm});
            skLineSegment(sketch, "E72.4.0.18", {"start": v(344, 30) * mm, "end": v(296, 30) * mm});
            skLineSegment(sketch, "E72.4.0.19", {"start": v(296, -27.25) * mm, "end": v(309, -27.25) * mm});
            skLineSegment(sketch, "E72.4.0.20", {"start": v(294, 14.17) * mm, "end": v(309.26, 18.26) * mm});
            skLineSegment(sketch, "E72.4.0.21", {"start": v(290, 24) * mm, "end": v(290, 11.88) * mm});
            skLineSegment(sketch, "E72.4.0.22", {"start": v(325.2, 25.2) * mm, "end": v(314.8, 25.2) * mm});
            skLineSegment(sketch, "E72.4.0.23", {"start": v(331.26, 15.27) * mm, "end": v(348.43, 10.67) * mm});
            skLineSegment(sketch, "E72.4.0.24", {"start": v(292.75, 24) * mm, "end": v(292.75, 15.14) * mm});
            skLineSegment(sketch, "E72.4.0.25", {"start": v(347.25, -24) * mm, "end": v(347.25, -15.14) * mm});
            skArc(sketch, "E72.4.0.26", {"start": v(313.6, 4.8) * mm, "mid": v(312, 0) * mm, "end": v(313.6, -4.8) * mm});
            skLineSegment(sketch, "E72.4.0.27", {"start": v(292.75, -15.14) * mm, "end": v(292.75, -24) * mm});
            skLineSegment(sketch, "E72.4.0.28", {"start": v(346, -14.17) * mm, "end": v(330.74, -18.26) * mm});
            skLineSegment(sketch, "E72.4.0.29", {"start": v(308.74, -15.27) * mm, "end": v(291.57, -10.67) * mm});
            skLineSegment(sketch, "E72.4.0.30", {"start": v(350, 11.88) * mm, "end": v(350, 24) * mm});
            skLineSegment(sketch, "E72.4.0.31", {"start": v(344, 27.25) * mm, "end": v(331, 27.25) * mm});
            skArc(sketch, "E72.4.0.32", {"start": v(326.4, -4.8) * mm, "mid": v(328, 0) * mm, "end": v(326.4, 4.8) * mm});
            skArc(sketch, "E72.4.0.33", {"start": v(290, -24) * mm, "mid": v(291.76, -28.24) * mm, "end": v(296, -30) * mm});
            skLineSegment(sketch, "E72.4.0.34", {"start": v(350, -24) * mm, "end": v(350, -11.88) * mm});
            skLineSegment(sketch, "E72.4.0.35", {"start": v(309, 27.25) * mm, "end": v(296, 27.25) * mm});
            skArc(sketch, "E72.4.0.36", {"start": v(325.2, -25.2) * mm, "mid": v(325.9, -24.9) * mm, "end": v(326.2, -24.2) * mm});
            skArc(sketch, "E72.4.0.37", {"start": v(292.75, -24) * mm, "mid": v(293.7, -26.3) * mm, "end": v(296, -27.25) * mm});
            skArc(sketch, "E72.4.0.38", {"start": v(347.25, -15.14) * mm, "mid": v(346.86, -14.34) * mm, "end": v(346, -14.17) * mm});
            skArc(sketch, "E72.4.0.39", {"start": v(330, -26.25) * mm, "mid": v(330.3, -26.96) * mm, "end": v(331, -27.25) * mm});
            skArc(sketch, "E72.4.0.40", {"start": v(326.2, 5.4) * mm, "mid": v(326.25, 5.08) * mm, "end": v(326.4, 4.8) * mm});
            skArc(sketch, "E72.4.0.41", {"start": v(344, -27.25) * mm, "mid": v(346.3, -26.3) * mm, "end": v(347.25, -24) * mm});
            skArc(sketch, "E72.4.0.42", {"start": v(313.6, 4.8) * mm, "mid": v(313.75, 5.08) * mm, "end": v(313.8, 5.4) * mm});
            skLineSegment(sketch, "E72.4.0.43", {"start": v(330, 26.25) * mm, "end": v(330, 19.22) * mm});
            skArc(sketch, "E72.4.0.44", {"start": v(350, -11.88) * mm, "mid": v(349.51, -10.89) * mm, "end": v(348.43, -10.67) * mm});
            skArc(sketch, "E72.4.0.45", {"start": v(330, -14.3) * mm, "mid": v(330.4, -15.1) * mm, "end": v(331.26, -15.27) * mm});
            skArc(sketch, "E72.4.0.46", {"start": v(331, 27.25) * mm, "mid": v(330.3, 26.96) * mm, "end": v(330, 26.25) * mm});
            skArc(sketch, "E72.4.0.47", {"start": v(296, 27.25) * mm, "mid": v(293.7, 26.3) * mm, "end": v(292.75, 24) * mm});
            skArc(sketch, "E72.4.0.48", {"start": v(346, 14.17) * mm, "mid": v(346.86, 14.34) * mm, "end": v(347.25, 15.14) * mm});
            skArc(sketch, "E72.4.0.49", {"start": v(348.43, 10.67) * mm, "mid": v(349.51, 10.89) * mm, "end": v(350, 11.88) * mm});
            skArc(sketch, "E72.4.0.50", {"start": v(330, 19.22) * mm, "mid": v(330.2, 18.61) * mm, "end": v(330.74, 18.26) * mm});
            skArc(sketch, "E72.4.0.51", {"start": v(331.26, 15.27) * mm, "mid": v(330.4, 15.1) * mm, "end": v(330, 14.3) * mm});
            skArc(sketch, "E72.4.0.52", {"start": v(347.25, 24) * mm, "mid": v(346.3, 26.3) * mm, "end": v(344, 27.25) * mm});
            skArc(sketch, "E72.4.0.53", {"start": v(291.57, -10.67) * mm, "mid": v(290.49, -10.89) * mm, "end": v(290, -11.88) * mm});
            skLineSegment(sketch, "E72.4.0.54", {"start": v(330, -19.22) * mm, "end": v(330, -26.25) * mm});
            skArc(sketch, "E72.4.0.55", {"start": v(313.8, -24.2) * mm, "mid": v(314.1, -24.9) * mm, "end": v(314.8, -25.2) * mm});
            skArc(sketch, "E72.4.0.56", {"start": v(330.74, -18.26) * mm, "mid": v(330.2, -18.61) * mm, "end": v(330, -19.22) * mm});
            skArc(sketch, "E72.4.0.57", {"start": v(294, -14.17) * mm, "mid": v(293.14, -14.34) * mm, "end": v(292.75, -15.14) * mm});
            skArc(sketch, "E72.4.0.58", {"start": v(290, 11.88) * mm, "mid": v(290.49, 10.89) * mm, "end": v(291.57, 10.67) * mm});
            skLineSegment(sketch, "E72.4.0.59", {"start": v(310, -26.25) * mm, "end": v(310, -19.22) * mm});
            skArc(sketch, "E72.4.0.60", {"start": v(309.26, 18.26) * mm, "mid": v(309.8, 18.61) * mm, "end": v(310, 19.22) * mm});
            skArc(sketch, "E72.4.0.61", {"start": v(326.2, 24.2) * mm, "mid": v(325.9, 24.9) * mm, "end": v(325.2, 25.2) * mm});
            skArc(sketch, "E72.4.0.62", {"start": v(292.75, 15.14) * mm, "mid": v(293.14, 14.34) * mm, "end": v(294, 14.17) * mm});
            skArc(sketch, "E72.4.0.63", {"start": v(310, -19.22) * mm, "mid": v(309.8, -18.61) * mm, "end": v(309.26, -18.26) * mm});
            skArc(sketch, "E72.4.0.64", {"start": v(314.8, 25.2) * mm, "mid": v(314.1, 24.9) * mm, "end": v(313.8, 24.2) * mm});
            skArc(sketch, "E72.4.0.65", {"start": v(310, 26.25) * mm, "mid": v(309.7, 26.96) * mm, "end": v(309, 27.25) * mm});
            skArc(sketch, "E72.4.0.66", {"start": v(310, 14.3) * mm, "mid": v(309.6, 15.1) * mm, "end": v(308.74, 15.27) * mm});
            skLineSegment(sketch, "E72.4.0.67", {"start": v(310, 19.22) * mm, "end": v(310, 26.25) * mm});
            skArc(sketch, "E72.4.0.68", {"start": v(308.74, -15.27) * mm, "mid": v(309.6, -15.1) * mm, "end": v(310, -14.3) * mm});
            skArc(sketch, "E72.4.0.69", {"start": v(309, -27.25) * mm, "mid": v(309.7, -26.96) * mm, "end": v(310, -26.25) * mm});
            skArc(sketch, "E72.4.0.70", {"start": v(326.4, -4.8) * mm, "mid": v(326.25, -5.08) * mm, "end": v(326.2, -5.4) * mm});
            skArc(sketch, "E72.4.0.71", {"start": v(313.8, -5.4) * mm, "mid": v(313.75, -5.08) * mm, "end": v(313.6, -4.8) * mm});
            skLineSegment(sketch, "E72.5.0.0", {"start": v(410.74, 18.26) * mm, "end": v(426, 14.17) * mm});
            skLineSegment(sketch, "E72.5.0.1", {"start": v(376, -30) * mm, "end": v(424, -30) * mm});
            skLineSegment(sketch, "E72.5.0.2", {"start": v(428.43, -10.67) * mm, "end": v(411.26, -15.27) * mm});
            skLineSegment(sketch, "E72.5.0.3", {"start": v(427.25, 15.14) * mm, "end": v(427.25, 24) * mm});
            skLineSegment(sketch, "E72.5.0.4", {"start": v(406.2, 5.4) * mm, "end": v(406.2, 24.2) * mm});
            skLineSegment(sketch, "E72.5.0.5", {"start": v(411, -27.25) * mm, "end": v(424, -27.25) * mm});
            skLineSegment(sketch, "E72.5.0.6", {"start": v(406.2, -24.2) * mm, "end": v(406.2, -5.4) * mm});
            skLineSegment(sketch, "E72.5.0.7", {"start": v(371.57, 10.67) * mm, "end": v(388.74, 15.27) * mm});
            skLineSegment(sketch, "E72.5.0.8", {"start": v(370, -11.88) * mm, "end": v(370, -24) * mm});
            skLineSegment(sketch, "E72.5.0.9", {"start": v(394.8, -25.2) * mm, "end": v(405.2, -25.2) * mm});
            skLineSegment(sketch, "E72.5.0.10", {"start": v(390, 14.3) * mm, "end": v(390, -14.3) * mm});
            skLineSegment(sketch, "E72.5.0.11", {"start": v(410, -14.3) * mm, "end": v(410, 14.3) * mm});
            skLineSegment(sketch, "E72.5.0.12", {"start": v(393.8, -5.4) * mm, "end": v(393.8, -24.2) * mm});
            skArc(sketch, "E72.5.0.13", {"start": v(376, 30) * mm, "mid": v(371.76, 28.24) * mm, "end": v(370, 24) * mm});
            skLineSegment(sketch, "E72.5.0.14", {"start": v(389.26, -18.26) * mm, "end": v(374, -14.17) * mm});
            skArc(sketch, "E72.5.0.15", {"start": v(430, 24) * mm, "mid": v(428.24, 28.24) * mm, "end": v(424, 30) * mm});
            skArc(sketch, "E72.5.0.16", {"start": v(424, -30) * mm, "mid": v(428.24, -28.24) * mm, "end": v(430, -24) * mm});
            skLineSegment(sketch, "E72.5.0.17", {"start": v(393.8, 24.2) * mm, "end": v(393.8, 5.4) * mm});
            skLineSegment(sketch, "E72.5.0.18", {"start": v(424, 30) * mm, "end": v(376, 30) * mm});
            skLineSegment(sketch, "E72.5.0.19", {"start": v(376, -27.25) * mm, "end": v(389, -27.25) * mm});
            skLineSegment(sketch, "E72.5.0.20", {"start": v(374, 14.17) * mm, "end": v(389.26, 18.26) * mm});
            skLineSegment(sketch, "E72.5.0.21", {"start": v(370, 24) * mm, "end": v(370, 11.88) * mm});
            skLineSegment(sketch, "E72.5.0.22", {"start": v(405.2, 25.2) * mm, "end": v(394.8, 25.2) * mm});
            skLineSegment(sketch, "E72.5.0.23", {"start": v(411.26, 15.27) * mm, "end": v(428.43, 10.67) * mm});
            skLineSegment(sketch, "E72.5.0.24", {"start": v(372.75, 24) * mm, "end": v(372.75, 15.14) * mm});
            skLineSegment(sketch, "E72.5.0.25", {"start": v(427.25, -24) * mm, "end": v(427.25, -15.14) * mm});
            skArc(sketch, "E72.5.0.26", {"start": v(393.6, 4.8) * mm, "mid": v(392, 0) * mm, "end": v(393.6, -4.8) * mm});
            skLineSegment(sketch, "E72.5.0.27", {"start": v(372.75, -15.14) * mm, "end": v(372.75, -24) * mm});
            skLineSegment(sketch, "E72.5.0.28", {"start": v(426, -14.17) * mm, "end": v(410.74, -18.26) * mm});
            skLineSegment(sketch, "E72.5.0.29", {"start": v(388.74, -15.27) * mm, "end": v(371.57, -10.67) * mm});
            skLineSegment(sketch, "E72.5.0.30", {"start": v(430, 11.88) * mm, "end": v(430, 24) * mm});
            skLineSegment(sketch, "E72.5.0.31", {"start": v(424, 27.25) * mm, "end": v(411, 27.25) * mm});
            skArc(sketch, "E72.5.0.32", {"start": v(406.4, -4.8) * mm, "mid": v(408, 0) * mm, "end": v(406.4, 4.8) * mm});
            skArc(sketch, "E72.5.0.33", {"start": v(370, -24) * mm, "mid": v(371.76, -28.24) * mm, "end": v(376, -30) * mm});
            skLineSegment(sketch, "E72.5.0.34", {"start": v(430, -24) * mm, "end": v(430, -11.88) * mm});
            skLineSegment(sketch, "E72.5.0.35", {"start": v(389, 27.25) * mm, "end": v(376, 27.25) * mm});
            skArc(sketch, "E72.5.0.36", {"start": v(405.2, -25.2) * mm, "mid": v(405.9, -24.9) * mm, "end": v(406.2, -24.2) * mm});
            skArc(sketch, "E72.5.0.37", {"start": v(372.75, -24) * mm, "mid": v(373.7, -26.3) * mm, "end": v(376, -27.25) * mm});
            skArc(sketch, "E72.5.0.38", {"start": v(427.25, -15.14) * mm, "mid": v(426.86, -14.34) * mm, "end": v(426, -14.17) * mm});
            skArc(sketch, "E72.5.0.39", {"start": v(410, -26.25) * mm, "mid": v(410.3, -26.96) * mm, "end": v(411, -27.25) * mm});
            skArc(sketch, "E72.5.0.40", {"start": v(406.2, 5.4) * mm, "mid": v(406.25, 5.08) * mm, "end": v(406.4, 4.8) * mm});
            skArc(sketch, "E72.5.0.41", {"start": v(424, -27.25) * mm, "mid": v(426.3, -26.3) * mm, "end": v(427.25, -24) * mm});
            skArc(sketch, "E72.5.0.42", {"start": v(393.6, 4.8) * mm, "mid": v(393.75, 5.08) * mm, "end": v(393.8, 5.4) * mm});
            skLineSegment(sketch, "E72.5.0.43", {"start": v(410, 26.25) * mm, "end": v(410, 19.22) * mm});
            skArc(sketch, "E72.5.0.44", {"start": v(430, -11.88) * mm, "mid": v(429.51, -10.89) * mm, "end": v(428.43, -10.67) * mm});
            skArc(sketch, "E72.5.0.45", {"start": v(410, -14.3) * mm, "mid": v(410.4, -15.1) * mm, "end": v(411.26, -15.27) * mm});
            skArc(sketch, "E72.5.0.46", {"start": v(411, 27.25) * mm, "mid": v(410.3, 26.96) * mm, "end": v(410, 26.25) * mm});
            skArc(sketch, "E72.5.0.47", {"start": v(376, 27.25) * mm, "mid": v(373.7, 26.3) * mm, "end": v(372.75, 24) * mm});
            skArc(sketch, "E72.5.0.48", {"start": v(426, 14.17) * mm, "mid": v(426.86, 14.34) * mm, "end": v(427.25, 15.14) * mm});
            skArc(sketch, "E72.5.0.49", {"start": v(428.43, 10.67) * mm, "mid": v(429.51, 10.89) * mm, "end": v(430, 11.88) * mm});
            skArc(sketch, "E72.5.0.50", {"start": v(410, 19.22) * mm, "mid": v(410.2, 18.61) * mm, "end": v(410.74, 18.26) * mm});
            skArc(sketch, "E72.5.0.51", {"start": v(411.26, 15.27) * mm, "mid": v(410.4, 15.1) * mm, "end": v(410, 14.3) * mm});
            skArc(sketch, "E72.5.0.52", {"start": v(427.25, 24) * mm, "mid": v(426.3, 26.3) * mm, "end": v(424, 27.25) * mm});
            skArc(sketch, "E72.5.0.53", {"start": v(371.57, -10.67) * mm, "mid": v(370.49, -10.89) * mm, "end": v(370, -11.88) * mm});
            skLineSegment(sketch, "E72.5.0.54", {"start": v(410, -19.22) * mm, "end": v(410, -26.25) * mm});
            skArc(sketch, "E72.5.0.55", {"start": v(393.8, -24.2) * mm, "mid": v(394.1, -24.9) * mm, "end": v(394.8, -25.2) * mm});
            skArc(sketch, "E72.5.0.56", {"start": v(410.74, -18.26) * mm, "mid": v(410.2, -18.61) * mm, "end": v(410, -19.22) * mm});
            skArc(sketch, "E72.5.0.57", {"start": v(374, -14.17) * mm, "mid": v(373.14, -14.34) * mm, "end": v(372.75, -15.14) * mm});
            skArc(sketch, "E72.5.0.58", {"start": v(370, 11.88) * mm, "mid": v(370.49, 10.89) * mm, "end": v(371.57, 10.67) * mm});
            skLineSegment(sketch, "E72.5.0.59", {"start": v(390, -26.25) * mm, "end": v(390, -19.22) * mm});
            skArc(sketch, "E72.5.0.60", {"start": v(389.26, 18.26) * mm, "mid": v(389.8, 18.61) * mm, "end": v(390, 19.22) * mm});
            skArc(sketch, "E72.5.0.61", {"start": v(406.2, 24.2) * mm, "mid": v(405.9, 24.9) * mm, "end": v(405.2, 25.2) * mm});
            skArc(sketch, "E72.5.0.62", {"start": v(372.75, 15.14) * mm, "mid": v(373.14, 14.34) * mm, "end": v(374, 14.17) * mm});
            skArc(sketch, "E72.5.0.63", {"start": v(390, -19.22) * mm, "mid": v(389.8, -18.61) * mm, "end": v(389.26, -18.26) * mm});
            skArc(sketch, "E72.5.0.64", {"start": v(394.8, 25.2) * mm, "mid": v(394.1, 24.9) * mm, "end": v(393.8, 24.2) * mm});
            skArc(sketch, "E72.5.0.65", {"start": v(390, 26.25) * mm, "mid": v(389.7, 26.96) * mm, "end": v(389, 27.25) * mm});
            skArc(sketch, "E72.5.0.66", {"start": v(390, 14.3) * mm, "mid": v(389.6, 15.1) * mm, "end": v(388.74, 15.27) * mm});
            skLineSegment(sketch, "E72.5.0.67", {"start": v(390, 19.22) * mm, "end": v(390, 26.25) * mm});
            skArc(sketch, "E72.5.0.68", {"start": v(388.74, -15.27) * mm, "mid": v(389.6, -15.1) * mm, "end": v(390, -14.3) * mm});
            skArc(sketch, "E72.5.0.69", {"start": v(389, -27.25) * mm, "mid": v(389.7, -26.96) * mm, "end": v(390, -26.25) * mm});
            skArc(sketch, "E72.5.0.70", {"start": v(406.4, -4.8) * mm, "mid": v(406.25, -5.08) * mm, "end": v(406.2, -5.4) * mm});
            skArc(sketch, "E72.5.0.71", {"start": v(393.8, -5.4) * mm, "mid": v(393.75, -5.08) * mm, "end": v(393.6, -4.8) * mm});
            skLineSegment(sketch, "E72.6.0.0", {"start": v(490.74, 18.26) * mm, "end": v(506, 14.17) * mm});
            skLineSegment(sketch, "E72.6.0.1", {"start": v(456, -30) * mm, "end": v(504, -30) * mm});
            skLineSegment(sketch, "E72.6.0.2", {"start": v(508.43, -10.67) * mm, "end": v(491.26, -15.27) * mm});
            skLineSegment(sketch, "E72.6.0.3", {"start": v(507.25, 15.14) * mm, "end": v(507.25, 24) * mm});
            skLineSegment(sketch, "E72.6.0.4", {"start": v(486.2, 5.4) * mm, "end": v(486.2, 24.2) * mm});
            skLineSegment(sketch, "E72.6.0.5", {"start": v(491, -27.25) * mm, "end": v(504, -27.25) * mm});
            skLineSegment(sketch, "E72.6.0.6", {"start": v(486.2, -24.2) * mm, "end": v(486.2, -5.4) * mm});
            skLineSegment(sketch, "E72.6.0.7", {"start": v(451.57, 10.67) * mm, "end": v(468.74, 15.27) * mm});
            skLineSegment(sketch, "E72.6.0.8", {"start": v(450, -11.88) * mm, "end": v(450, -24) * mm});
            skLineSegment(sketch, "E72.6.0.9", {"start": v(474.8, -25.2) * mm, "end": v(485.2, -25.2) * mm});
            skLineSegment(sketch, "E72.6.0.10", {"start": v(470, 14.3) * mm, "end": v(470, -14.3) * mm});
            skLineSegment(sketch, "E72.6.0.11", {"start": v(490, -14.3) * mm, "end": v(490, 14.3) * mm});
            skLineSegment(sketch, "E72.6.0.12", {"start": v(473.8, -5.4) * mm, "end": v(473.8, -24.2) * mm});
            skArc(sketch, "E72.6.0.13", {"start": v(456, 30) * mm, "mid": v(451.76, 28.24) * mm, "end": v(450, 24) * mm});
            skLineSegment(sketch, "E72.6.0.14", {"start": v(469.26, -18.26) * mm, "end": v(454, -14.17) * mm});
            skArc(sketch, "E72.6.0.15", {"start": v(510, 24) * mm, "mid": v(508.24, 28.24) * mm, "end": v(504, 30) * mm});
            skArc(sketch, "E72.6.0.16", {"start": v(504, -30) * mm, "mid": v(508.24, -28.24) * mm, "end": v(510, -24) * mm});
            skLineSegment(sketch, "E72.6.0.17", {"start": v(473.8, 24.2) * mm, "end": v(473.8, 5.4) * mm});
            skLineSegment(sketch, "E72.6.0.18", {"start": v(504, 30) * mm, "end": v(456, 30) * mm});
            skLineSegment(sketch, "E72.6.0.19", {"start": v(456, -27.25) * mm, "end": v(469, -27.25) * mm});
            skLineSegment(sketch, "E72.6.0.20", {"start": v(454, 14.17) * mm, "end": v(469.26, 18.26) * mm});
            skLineSegment(sketch, "E72.6.0.21", {"start": v(450, 24) * mm, "end": v(450, 11.88) * mm});
            skLineSegment(sketch, "E72.6.0.22", {"start": v(485.2, 25.2) * mm, "end": v(474.8, 25.2) * mm});
            skLineSegment(sketch, "E72.6.0.23", {"start": v(491.26, 15.27) * mm, "end": v(508.43, 10.67) * mm});
            skLineSegment(sketch, "E72.6.0.24", {"start": v(452.75, 24) * mm, "end": v(452.75, 15.14) * mm});
            skLineSegment(sketch, "E72.6.0.25", {"start": v(507.25, -24) * mm, "end": v(507.25, -15.14) * mm});
            skArc(sketch, "E72.6.0.26", {"start": v(473.6, 4.8) * mm, "mid": v(472, 0) * mm, "end": v(473.6, -4.8) * mm});
            skLineSegment(sketch, "E72.6.0.27", {"start": v(452.75, -15.14) * mm, "end": v(452.75, -24) * mm});
            skLineSegment(sketch, "E72.6.0.28", {"start": v(506, -14.17) * mm, "end": v(490.74, -18.26) * mm});
            skLineSegment(sketch, "E72.6.0.29", {"start": v(468.74, -15.27) * mm, "end": v(451.57, -10.67) * mm});
            skLineSegment(sketch, "E72.6.0.30", {"start": v(510, 11.88) * mm, "end": v(510, 24) * mm});
            skLineSegment(sketch, "E72.6.0.31", {"start": v(504, 27.25) * mm, "end": v(491, 27.25) * mm});
            skArc(sketch, "E72.6.0.32", {"start": v(486.4, -4.8) * mm, "mid": v(488, 0) * mm, "end": v(486.4, 4.8) * mm});
            skArc(sketch, "E72.6.0.33", {"start": v(450, -24) * mm, "mid": v(451.76, -28.24) * mm, "end": v(456, -30) * mm});
            skLineSegment(sketch, "E72.6.0.34", {"start": v(510, -24) * mm, "end": v(510, -11.88) * mm});
            skLineSegment(sketch, "E72.6.0.35", {"start": v(469, 27.25) * mm, "end": v(456, 27.25) * mm});
            skArc(sketch, "E72.6.0.36", {"start": v(485.2, -25.2) * mm, "mid": v(485.9, -24.9) * mm, "end": v(486.2, -24.2) * mm});
            skArc(sketch, "E72.6.0.37", {"start": v(452.75, -24) * mm, "mid": v(453.7, -26.3) * mm, "end": v(456, -27.25) * mm});
            skArc(sketch, "E72.6.0.38", {"start": v(507.25, -15.14) * mm, "mid": v(506.86, -14.34) * mm, "end": v(506, -14.17) * mm});
            skArc(sketch, "E72.6.0.39", {"start": v(490, -26.25) * mm, "mid": v(490.3, -26.96) * mm, "end": v(491, -27.25) * mm});
            skArc(sketch, "E72.6.0.40", {"start": v(486.2, 5.4) * mm, "mid": v(486.25, 5.08) * mm, "end": v(486.4, 4.8) * mm});
            skArc(sketch, "E72.6.0.41", {"start": v(504, -27.25) * mm, "mid": v(506.3, -26.3) * mm, "end": v(507.25, -24) * mm});
            skArc(sketch, "E72.6.0.42", {"start": v(473.6, 4.8) * mm, "mid": v(473.75, 5.08) * mm, "end": v(473.8, 5.4) * mm});
            skLineSegment(sketch, "E72.6.0.43", {"start": v(490, 26.25) * mm, "end": v(490, 19.22) * mm});
            skArc(sketch, "E72.6.0.44", {"start": v(510, -11.88) * mm, "mid": v(509.51, -10.89) * mm, "end": v(508.43, -10.67) * mm});
            skArc(sketch, "E72.6.0.45", {"start": v(490, -14.3) * mm, "mid": v(490.4, -15.1) * mm, "end": v(491.26, -15.27) * mm});
            skArc(sketch, "E72.6.0.46", {"start": v(491, 27.25) * mm, "mid": v(490.3, 26.96) * mm, "end": v(490, 26.25) * mm});
            skArc(sketch, "E72.6.0.47", {"start": v(456, 27.25) * mm, "mid": v(453.7, 26.3) * mm, "end": v(452.75, 24) * mm});
            skArc(sketch, "E72.6.0.48", {"start": v(506, 14.17) * mm, "mid": v(506.86, 14.34) * mm, "end": v(507.25, 15.14) * mm});
            skArc(sketch, "E72.6.0.49", {"start": v(508.43, 10.67) * mm, "mid": v(509.51, 10.89) * mm, "end": v(510, 11.88) * mm});
            skArc(sketch, "E72.6.0.50", {"start": v(490, 19.22) * mm, "mid": v(490.2, 18.61) * mm, "end": v(490.74, 18.26) * mm});
            skArc(sketch, "E72.6.0.51", {"start": v(491.26, 15.27) * mm, "mid": v(490.4, 15.1) * mm, "end": v(490, 14.3) * mm});
            skArc(sketch, "E72.6.0.52", {"start": v(507.25, 24) * mm, "mid": v(506.3, 26.3) * mm, "end": v(504, 27.25) * mm});
            skArc(sketch, "E72.6.0.53", {"start": v(451.57, -10.67) * mm, "mid": v(450.49, -10.89) * mm, "end": v(450, -11.88) * mm});
            skLineSegment(sketch, "E72.6.0.54", {"start": v(490, -19.22) * mm, "end": v(490, -26.25) * mm});
            skArc(sketch, "E72.6.0.55", {"start": v(473.8, -24.2) * mm, "mid": v(474.1, -24.9) * mm, "end": v(474.8, -25.2) * mm});
            skArc(sketch, "E72.6.0.56", {"start": v(490.74, -18.26) * mm, "mid": v(490.2, -18.61) * mm, "end": v(490, -19.22) * mm});
            skArc(sketch, "E72.6.0.57", {"start": v(454, -14.17) * mm, "mid": v(453.14, -14.34) * mm, "end": v(452.75, -15.14) * mm});
            skArc(sketch, "E72.6.0.58", {"start": v(450, 11.88) * mm, "mid": v(450.49, 10.89) * mm, "end": v(451.57, 10.67) * mm});
            skLineSegment(sketch, "E72.6.0.59", {"start": v(470, -26.25) * mm, "end": v(470, -19.22) * mm});
            skArc(sketch, "E72.6.0.60", {"start": v(469.26, 18.26) * mm, "mid": v(469.8, 18.61) * mm, "end": v(470, 19.22) * mm});
            skArc(sketch, "E72.6.0.61", {"start": v(486.2, 24.2) * mm, "mid": v(485.9, 24.9) * mm, "end": v(485.2, 25.2) * mm});
            skArc(sketch, "E72.6.0.62", {"start": v(452.75, 15.14) * mm, "mid": v(453.14, 14.34) * mm, "end": v(454, 14.17) * mm});
            skArc(sketch, "E72.6.0.63", {"start": v(470, -19.22) * mm, "mid": v(469.8, -18.61) * mm, "end": v(469.26, -18.26) * mm});
            skArc(sketch, "E72.6.0.64", {"start": v(474.8, 25.2) * mm, "mid": v(474.1, 24.9) * mm, "end": v(473.8, 24.2) * mm});
            skArc(sketch, "E72.6.0.65", {"start": v(470, 26.25) * mm, "mid": v(469.7, 26.96) * mm, "end": v(469, 27.25) * mm});
            skArc(sketch, "E72.6.0.66", {"start": v(470, 14.3) * mm, "mid": v(469.6, 15.1) * mm, "end": v(468.74, 15.27) * mm});
            skLineSegment(sketch, "E72.6.0.67", {"start": v(470, 19.22) * mm, "end": v(470, 26.25) * mm});
            skArc(sketch, "E72.6.0.68", {"start": v(468.74, -15.27) * mm, "mid": v(469.6, -15.1) * mm, "end": v(470, -14.3) * mm});
            skArc(sketch, "E72.6.0.69", {"start": v(469, -27.25) * mm, "mid": v(469.7, -26.96) * mm, "end": v(470, -26.25) * mm});
            skArc(sketch, "E72.6.0.70", {"start": v(486.4, -4.8) * mm, "mid": v(486.25, -5.08) * mm, "end": v(486.2, -5.4) * mm});
            skArc(sketch, "E72.6.0.71", {"start": v(473.8, -5.4) * mm, "mid": v(473.75, -5.08) * mm, "end": v(473.6, -4.8) * mm});
            skLineSegment(sketch, "E72.7.0.0", {"start": v(570.74, 18.26) * mm, "end": v(586, 14.17) * mm});
            skLineSegment(sketch, "E72.7.0.1", {"start": v(536, -30) * mm, "end": v(584, -30) * mm});
            skLineSegment(sketch, "E72.7.0.2", {"start": v(588.43, -10.67) * mm, "end": v(571.26, -15.27) * mm});
            skLineSegment(sketch, "E72.7.0.3", {"start": v(587.25, 15.14) * mm, "end": v(587.25, 24) * mm});
            skLineSegment(sketch, "E72.7.0.4", {"start": v(566.2, 5.4) * mm, "end": v(566.2, 24.2) * mm});
            skLineSegment(sketch, "E72.7.0.5", {"start": v(571, -27.25) * mm, "end": v(584, -27.25) * mm});
            skLineSegment(sketch, "E72.7.0.6", {"start": v(566.2, -24.2) * mm, "end": v(566.2, -5.4) * mm});
            skLineSegment(sketch, "E72.7.0.7", {"start": v(531.57, 10.67) * mm, "end": v(548.74, 15.27) * mm});
            skLineSegment(sketch, "E72.7.0.8", {"start": v(530, -11.88) * mm, "end": v(530, -24) * mm});
            skLineSegment(sketch, "E72.7.0.9", {"start": v(554.8, -25.2) * mm, "end": v(565.2, -25.2) * mm});
            skLineSegment(sketch, "E72.7.0.10", {"start": v(550, 14.3) * mm, "end": v(550, -14.3) * mm});
            skLineSegment(sketch, "E72.7.0.11", {"start": v(570, -14.3) * mm, "end": v(570, 14.3) * mm});
            skLineSegment(sketch, "E72.7.0.12", {"start": v(553.8, -5.4) * mm, "end": v(553.8, -24.2) * mm});
            skArc(sketch, "E72.7.0.13", {"start": v(536, 30) * mm, "mid": v(531.76, 28.24) * mm, "end": v(530, 24) * mm});
            skLineSegment(sketch, "E72.7.0.14", {"start": v(549.26, -18.26) * mm, "end": v(534, -14.17) * mm});
            skArc(sketch, "E72.7.0.15", {"start": v(590, 24) * mm, "mid": v(588.24, 28.24) * mm, "end": v(584, 30) * mm});
            skArc(sketch, "E72.7.0.16", {"start": v(584, -30) * mm, "mid": v(588.24, -28.24) * mm, "end": v(590, -24) * mm});
            skLineSegment(sketch, "E72.7.0.17", {"start": v(553.8, 24.2) * mm, "end": v(553.8, 5.4) * mm});
            skLineSegment(sketch, "E72.7.0.18", {"start": v(584, 30) * mm, "end": v(536, 30) * mm});
            skLineSegment(sketch, "E72.7.0.19", {"start": v(536, -27.25) * mm, "end": v(549, -27.25) * mm});
            skLineSegment(sketch, "E72.7.0.20", {"start": v(534, 14.17) * mm, "end": v(549.26, 18.26) * mm});
            skLineSegment(sketch, "E72.7.0.21", {"start": v(530, 24) * mm, "end": v(530, 11.88) * mm});
            skLineSegment(sketch, "E72.7.0.22", {"start": v(565.2, 25.2) * mm, "end": v(554.8, 25.2) * mm});
            skLineSegment(sketch, "E72.7.0.23", {"start": v(571.26, 15.27) * mm, "end": v(588.43, 10.67) * mm});
            skLineSegment(sketch, "E72.7.0.24", {"start": v(532.75, 24) * mm, "end": v(532.75, 15.14) * mm});
            skLineSegment(sketch, "E72.7.0.25", {"start": v(587.25, -24) * mm, "end": v(587.25, -15.14) * mm});
            skArc(sketch, "E72.7.0.26", {"start": v(553.6, 4.8) * mm, "mid": v(552, 0) * mm, "end": v(553.6, -4.8) * mm});
            skLineSegment(sketch, "E72.7.0.27", {"start": v(532.75, -15.14) * mm, "end": v(532.75, -24) * mm});
            skLineSegment(sketch, "E72.7.0.28", {"start": v(586, -14.17) * mm, "end": v(570.74, -18.26) * mm});
            skLineSegment(sketch, "E72.7.0.29", {"start": v(548.74, -15.27) * mm, "end": v(531.57, -10.67) * mm});
            skLineSegment(sketch, "E72.7.0.30", {"start": v(590, 11.88) * mm, "end": v(590, 24) * mm});
            skLineSegment(sketch, "E72.7.0.31", {"start": v(584, 27.25) * mm, "end": v(571, 27.25) * mm});
            skArc(sketch, "E72.7.0.32", {"start": v(566.4, -4.8) * mm, "mid": v(568, 0) * mm, "end": v(566.4, 4.8) * mm});
            skArc(sketch, "E72.7.0.33", {"start": v(530, -24) * mm, "mid": v(531.76, -28.24) * mm, "end": v(536, -30) * mm});
            skLineSegment(sketch, "E72.7.0.34", {"start": v(590, -24) * mm, "end": v(590, -11.88) * mm});
            skLineSegment(sketch, "E72.7.0.35", {"start": v(549, 27.25) * mm, "end": v(536, 27.25) * mm});
            skArc(sketch, "E72.7.0.36", {"start": v(565.2, -25.2) * mm, "mid": v(565.9, -24.9) * mm, "end": v(566.2, -24.2) * mm});
            skArc(sketch, "E72.7.0.37", {"start": v(532.75, -24) * mm, "mid": v(533.7, -26.3) * mm, "end": v(536, -27.25) * mm});
            skArc(sketch, "E72.7.0.38", {"start": v(587.25, -15.14) * mm, "mid": v(586.86, -14.34) * mm, "end": v(586, -14.17) * mm});
            skArc(sketch, "E72.7.0.39", {"start": v(570, -26.25) * mm, "mid": v(570.3, -26.96) * mm, "end": v(571, -27.25) * mm});
            skArc(sketch, "E72.7.0.40", {"start": v(566.2, 5.4) * mm, "mid": v(566.25, 5.08) * mm, "end": v(566.4, 4.8) * mm});
            skArc(sketch, "E72.7.0.41", {"start": v(584, -27.25) * mm, "mid": v(586.3, -26.3) * mm, "end": v(587.25, -24) * mm});
            skArc(sketch, "E72.7.0.42", {"start": v(553.6, 4.8) * mm, "mid": v(553.75, 5.08) * mm, "end": v(553.8, 5.4) * mm});
            skLineSegment(sketch, "E72.7.0.43", {"start": v(570, 26.25) * mm, "end": v(570, 19.22) * mm});
            skArc(sketch, "E72.7.0.44", {"start": v(590, -11.88) * mm, "mid": v(589.51, -10.89) * mm, "end": v(588.43, -10.67) * mm});
            skArc(sketch, "E72.7.0.45", {"start": v(570, -14.3) * mm, "mid": v(570.4, -15.1) * mm, "end": v(571.26, -15.27) * mm});
            skArc(sketch, "E72.7.0.46", {"start": v(571, 27.25) * mm, "mid": v(570.3, 26.96) * mm, "end": v(570, 26.25) * mm});
            skArc(sketch, "E72.7.0.47", {"start": v(536, 27.25) * mm, "mid": v(533.7, 26.3) * mm, "end": v(532.75, 24) * mm});
            skArc(sketch, "E72.7.0.48", {"start": v(586, 14.17) * mm, "mid": v(586.86, 14.34) * mm, "end": v(587.25, 15.14) * mm});
            skArc(sketch, "E72.7.0.49", {"start": v(588.43, 10.67) * mm, "mid": v(589.51, 10.89) * mm, "end": v(590, 11.88) * mm});
            skArc(sketch, "E72.7.0.50", {"start": v(570, 19.22) * mm, "mid": v(570.2, 18.61) * mm, "end": v(570.74, 18.26) * mm});
            skArc(sketch, "E72.7.0.51", {"start": v(571.26, 15.27) * mm, "mid": v(570.4, 15.1) * mm, "end": v(570, 14.3) * mm});
            skArc(sketch, "E72.7.0.52", {"start": v(587.25, 24) * mm, "mid": v(586.3, 26.3) * mm, "end": v(584, 27.25) * mm});
            skArc(sketch, "E72.7.0.53", {"start": v(531.57, -10.67) * mm, "mid": v(530.49, -10.89) * mm, "end": v(530, -11.88) * mm});
            skLineSegment(sketch, "E72.7.0.54", {"start": v(570, -19.22) * mm, "end": v(570, -26.25) * mm});
            skArc(sketch, "E72.7.0.55", {"start": v(553.8, -24.2) * mm, "mid": v(554.1, -24.9) * mm, "end": v(554.8, -25.2) * mm});
            skArc(sketch, "E72.7.0.56", {"start": v(570.74, -18.26) * mm, "mid": v(570.2, -18.61) * mm, "end": v(570, -19.22) * mm});
            skArc(sketch, "E72.7.0.57", {"start": v(534, -14.17) * mm, "mid": v(533.14, -14.34) * mm, "end": v(532.75, -15.14) * mm});
            skArc(sketch, "E72.7.0.58", {"start": v(530, 11.88) * mm, "mid": v(530.49, 10.89) * mm, "end": v(531.57, 10.67) * mm});
            skLineSegment(sketch, "E72.7.0.59", {"start": v(550, -26.25) * mm, "end": v(550, -19.22) * mm});
            skArc(sketch, "E72.7.0.60", {"start": v(549.26, 18.26) * mm, "mid": v(549.8, 18.61) * mm, "end": v(550, 19.22) * mm});
            skArc(sketch, "E72.7.0.61", {"start": v(566.2, 24.2) * mm, "mid": v(565.9, 24.9) * mm, "end": v(565.2, 25.2) * mm});
            skArc(sketch, "E72.7.0.62", {"start": v(532.75, 15.14) * mm, "mid": v(533.14, 14.34) * mm, "end": v(534, 14.17) * mm});
            skArc(sketch, "E72.7.0.63", {"start": v(550, -19.22) * mm, "mid": v(549.8, -18.61) * mm, "end": v(549.26, -18.26) * mm});
            skArc(sketch, "E72.7.0.64", {"start": v(554.8, 25.2) * mm, "mid": v(554.1, 24.9) * mm, "end": v(553.8, 24.2) * mm});
            skArc(sketch, "E72.7.0.65", {"start": v(550, 26.25) * mm, "mid": v(549.7, 26.96) * mm, "end": v(549, 27.25) * mm});
            skArc(sketch, "E72.7.0.66", {"start": v(550, 14.3) * mm, "mid": v(549.6, 15.1) * mm, "end": v(548.74, 15.27) * mm});
            skLineSegment(sketch, "E72.7.0.67", {"start": v(550, 19.22) * mm, "end": v(550, 26.25) * mm});
            skArc(sketch, "E72.7.0.68", {"start": v(548.74, -15.27) * mm, "mid": v(549.6, -15.1) * mm, "end": v(550, -14.3) * mm});
            skArc(sketch, "E72.7.0.69", {"start": v(549, -27.25) * mm, "mid": v(549.7, -26.96) * mm, "end": v(550, -26.25) * mm});
            skArc(sketch, "E72.7.0.70", {"start": v(566.4, -4.8) * mm, "mid": v(566.25, -5.08) * mm, "end": v(566.2, -5.4) * mm});
            skArc(sketch, "E72.7.0.71", {"start": v(553.8, -5.4) * mm, "mid": v(553.75, -5.08) * mm, "end": v(553.6, -4.8) * mm});
            skLineSegment(sketch, "E72.8.0.0", {"start": v(650.74, 18.26) * mm, "end": v(666, 14.17) * mm});
            skLineSegment(sketch, "E72.8.0.1", {"start": v(616, -30) * mm, "end": v(664, -30) * mm});
            skLineSegment(sketch, "E72.8.0.2", {"start": v(668.43, -10.67) * mm, "end": v(651.26, -15.27) * mm});
            skLineSegment(sketch, "E72.8.0.3", {"start": v(667.25, 15.14) * mm, "end": v(667.25, 24) * mm});
            skLineSegment(sketch, "E72.8.0.4", {"start": v(646.2, 5.4) * mm, "end": v(646.2, 24.2) * mm});
            skLineSegment(sketch, "E72.8.0.5", {"start": v(651, -27.25) * mm, "end": v(664, -27.25) * mm});
            skLineSegment(sketch, "E72.8.0.6", {"start": v(646.2, -24.2) * mm, "end": v(646.2, -5.4) * mm});
            skLineSegment(sketch, "E72.8.0.7", {"start": v(611.57, 10.67) * mm, "end": v(628.74, 15.27) * mm});
            skLineSegment(sketch, "E72.8.0.8", {"start": v(610, -11.88) * mm, "end": v(610, -24) * mm});
            skLineSegment(sketch, "E72.8.0.9", {"start": v(634.8, -25.2) * mm, "end": v(645.2, -25.2) * mm});
            skLineSegment(sketch, "E72.8.0.10", {"start": v(630, 14.3) * mm, "end": v(630, -14.3) * mm});
            skLineSegment(sketch, "E72.8.0.11", {"start": v(650, -14.3) * mm, "end": v(650, 14.3) * mm});
            skLineSegment(sketch, "E72.8.0.12", {"start": v(633.8, -5.4) * mm, "end": v(633.8, -24.2) * mm});
            skArc(sketch, "E72.8.0.13", {"start": v(616, 30) * mm, "mid": v(611.76, 28.24) * mm, "end": v(610, 24) * mm});
            skLineSegment(sketch, "E72.8.0.14", {"start": v(629.26, -18.26) * mm, "end": v(614, -14.17) * mm});
            skArc(sketch, "E72.8.0.15", {"start": v(670, 24) * mm, "mid": v(668.24, 28.24) * mm, "end": v(664, 30) * mm});
            skArc(sketch, "E72.8.0.16", {"start": v(664, -30) * mm, "mid": v(668.24, -28.24) * mm, "end": v(670, -24) * mm});
            skLineSegment(sketch, "E72.8.0.17", {"start": v(633.8, 24.2) * mm, "end": v(633.8, 5.4) * mm});
            skLineSegment(sketch, "E72.8.0.18", {"start": v(664, 30) * mm, "end": v(616, 30) * mm});
            skLineSegment(sketch, "E72.8.0.19", {"start": v(616, -27.25) * mm, "end": v(629, -27.25) * mm});
            skLineSegment(sketch, "E72.8.0.20", {"start": v(614, 14.17) * mm, "end": v(629.26, 18.26) * mm});
            skLineSegment(sketch, "E72.8.0.21", {"start": v(610, 24) * mm, "end": v(610, 11.88) * mm});
            skLineSegment(sketch, "E72.8.0.22", {"start": v(645.2, 25.2) * mm, "end": v(634.8, 25.2) * mm});
            skLineSegment(sketch, "E72.8.0.23", {"start": v(651.26, 15.27) * mm, "end": v(668.43, 10.67) * mm});
            skLineSegment(sketch, "E72.8.0.24", {"start": v(612.75, 24) * mm, "end": v(612.75, 15.14) * mm});
            skLineSegment(sketch, "E72.8.0.25", {"start": v(667.25, -24) * mm, "end": v(667.25, -15.14) * mm});
            skArc(sketch, "E72.8.0.26", {"start": v(633.6, 4.8) * mm, "mid": v(632, 0) * mm, "end": v(633.6, -4.8) * mm});
            skLineSegment(sketch, "E72.8.0.27", {"start": v(612.75, -15.14) * mm, "end": v(612.75, -24) * mm});
            skLineSegment(sketch, "E72.8.0.28", {"start": v(666, -14.17) * mm, "end": v(650.74, -18.26) * mm});
            skLineSegment(sketch, "E72.8.0.29", {"start": v(628.74, -15.27) * mm, "end": v(611.57, -10.67) * mm});
            skLineSegment(sketch, "E72.8.0.30", {"start": v(670, 11.88) * mm, "end": v(670, 24) * mm});
            skLineSegment(sketch, "E72.8.0.31", {"start": v(664, 27.25) * mm, "end": v(651, 27.25) * mm});
            skArc(sketch, "E72.8.0.32", {"start": v(646.4, -4.8) * mm, "mid": v(648, 0) * mm, "end": v(646.4, 4.8) * mm});
            skArc(sketch, "E72.8.0.33", {"start": v(610, -24) * mm, "mid": v(611.76, -28.24) * mm, "end": v(616, -30) * mm});
            skLineSegment(sketch, "E72.8.0.34", {"start": v(670, -24) * mm, "end": v(670, -11.88) * mm});
            skLineSegment(sketch, "E72.8.0.35", {"start": v(629, 27.25) * mm, "end": v(616, 27.25) * mm});
            skArc(sketch, "E72.8.0.36", {"start": v(645.2, -25.2) * mm, "mid": v(645.9, -24.9) * mm, "end": v(646.2, -24.2) * mm});
            skArc(sketch, "E72.8.0.37", {"start": v(612.75, -24) * mm, "mid": v(613.7, -26.3) * mm, "end": v(616, -27.25) * mm});
            skArc(sketch, "E72.8.0.38", {"start": v(667.25, -15.14) * mm, "mid": v(666.86, -14.34) * mm, "end": v(666, -14.17) * mm});
            skArc(sketch, "E72.8.0.39", {"start": v(650, -26.25) * mm, "mid": v(650.3, -26.96) * mm, "end": v(651, -27.25) * mm});
            skArc(sketch, "E72.8.0.40", {"start": v(646.2, 5.4) * mm, "mid": v(646.25, 5.08) * mm, "end": v(646.4, 4.8) * mm});
            skArc(sketch, "E72.8.0.41", {"start": v(664, -27.25) * mm, "mid": v(666.3, -26.3) * mm, "end": v(667.25, -24) * mm});
            skArc(sketch, "E72.8.0.42", {"start": v(633.6, 4.8) * mm, "mid": v(633.75, 5.08) * mm, "end": v(633.8, 5.4) * mm});
            skLineSegment(sketch, "E72.8.0.43", {"start": v(650, 26.25) * mm, "end": v(650, 19.22) * mm});
            skArc(sketch, "E72.8.0.44", {"start": v(670, -11.88) * mm, "mid": v(669.51, -10.89) * mm, "end": v(668.43, -10.67) * mm});
            skArc(sketch, "E72.8.0.45", {"start": v(650, -14.3) * mm, "mid": v(650.4, -15.1) * mm, "end": v(651.26, -15.27) * mm});
            skArc(sketch, "E72.8.0.46", {"start": v(651, 27.25) * mm, "mid": v(650.3, 26.96) * mm, "end": v(650, 26.25) * mm});
            skArc(sketch, "E72.8.0.47", {"start": v(616, 27.25) * mm, "mid": v(613.7, 26.3) * mm, "end": v(612.75, 24) * mm});
            skArc(sketch, "E72.8.0.48", {"start": v(666, 14.17) * mm, "mid": v(666.86, 14.34) * mm, "end": v(667.25, 15.14) * mm});
            skArc(sketch, "E72.8.0.49", {"start": v(668.43, 10.67) * mm, "mid": v(669.51, 10.89) * mm, "end": v(670, 11.88) * mm});
            skArc(sketch, "E72.8.0.50", {"start": v(650, 19.22) * mm, "mid": v(650.2, 18.61) * mm, "end": v(650.74, 18.26) * mm});
            skArc(sketch, "E72.8.0.51", {"start": v(651.26, 15.27) * mm, "mid": v(650.4, 15.1) * mm, "end": v(650, 14.3) * mm});
            skArc(sketch, "E72.8.0.52", {"start": v(667.25, 24) * mm, "mid": v(666.3, 26.3) * mm, "end": v(664, 27.25) * mm});
            skArc(sketch, "E72.8.0.53", {"start": v(611.57, -10.67) * mm, "mid": v(610.49, -10.89) * mm, "end": v(610, -11.88) * mm});
            skLineSegment(sketch, "E72.8.0.54", {"start": v(650, -19.22) * mm, "end": v(650, -26.25) * mm});
            skArc(sketch, "E72.8.0.55", {"start": v(633.8, -24.2) * mm, "mid": v(634.1, -24.9) * mm, "end": v(634.8, -25.2) * mm});
            skArc(sketch, "E72.8.0.56", {"start": v(650.74, -18.26) * mm, "mid": v(650.2, -18.61) * mm, "end": v(650, -19.22) * mm});
            skArc(sketch, "E72.8.0.57", {"start": v(614, -14.17) * mm, "mid": v(613.14, -14.34) * mm, "end": v(612.75, -15.14) * mm});
            skArc(sketch, "E72.8.0.58", {"start": v(610, 11.88) * mm, "mid": v(610.49, 10.89) * mm, "end": v(611.57, 10.67) * mm});
            skLineSegment(sketch, "E72.8.0.59", {"start": v(630, -26.25) * mm, "end": v(630, -19.22) * mm});
            skArc(sketch, "E72.8.0.60", {"start": v(629.26, 18.26) * mm, "mid": v(629.8, 18.61) * mm, "end": v(630, 19.22) * mm});
            skArc(sketch, "E72.8.0.61", {"start": v(646.2, 24.2) * mm, "mid": v(645.9, 24.9) * mm, "end": v(645.2, 25.2) * mm});
            skArc(sketch, "E72.8.0.62", {"start": v(612.75, 15.14) * mm, "mid": v(613.14, 14.34) * mm, "end": v(614, 14.17) * mm});
            skArc(sketch, "E72.8.0.63", {"start": v(630, -19.22) * mm, "mid": v(629.8, -18.61) * mm, "end": v(629.26, -18.26) * mm});
            skArc(sketch, "E72.8.0.64", {"start": v(634.8, 25.2) * mm, "mid": v(634.1, 24.9) * mm, "end": v(633.8, 24.2) * mm});
            skArc(sketch, "E72.8.0.65", {"start": v(630, 26.25) * mm, "mid": v(629.7, 26.96) * mm, "end": v(629, 27.25) * mm});
            skArc(sketch, "E72.8.0.66", {"start": v(630, 14.3) * mm, "mid": v(629.6, 15.1) * mm, "end": v(628.74, 15.27) * mm});
            skLineSegment(sketch, "E72.8.0.67", {"start": v(630, 19.22) * mm, "end": v(630, 26.25) * mm});
            skArc(sketch, "E72.8.0.68", {"start": v(628.74, -15.27) * mm, "mid": v(629.6, -15.1) * mm, "end": v(630, -14.3) * mm});
            skArc(sketch, "E72.8.0.69", {"start": v(629, -27.25) * mm, "mid": v(629.7, -26.96) * mm, "end": v(630, -26.25) * mm});
            skArc(sketch, "E72.8.0.70", {"start": v(646.4, -4.8) * mm, "mid": v(646.25, -5.08) * mm, "end": v(646.2, -5.4) * mm});
            skArc(sketch, "E72.8.0.71", {"start": v(633.8, -5.4) * mm, "mid": v(633.75, -5.08) * mm, "end": v(633.6, -4.8) * mm});
            skLineSegment(sketch, "E72.9.0.0", {"start": v(730.74, 18.26) * mm, "end": v(746, 14.17) * mm});
            skLineSegment(sketch, "E72.9.0.1", {"start": v(696, -30) * mm, "end": v(744, -30) * mm});
            skLineSegment(sketch, "E72.9.0.2", {"start": v(748.43, -10.67) * mm, "end": v(731.26, -15.27) * mm});
            skLineSegment(sketch, "E72.9.0.3", {"start": v(747.25, 15.14) * mm, "end": v(747.25, 24) * mm});
            skLineSegment(sketch, "E72.9.0.4", {"start": v(726.2, 5.4) * mm, "end": v(726.2, 24.2) * mm});
            skLineSegment(sketch, "E72.9.0.5", {"start": v(731, -27.25) * mm, "end": v(744, -27.25) * mm});
            skLineSegment(sketch, "E72.9.0.6", {"start": v(726.2, -24.2) * mm, "end": v(726.2, -5.4) * mm});
            skLineSegment(sketch, "E72.9.0.7", {"start": v(691.57, 10.67) * mm, "end": v(708.74, 15.27) * mm});
            skLineSegment(sketch, "E72.9.0.8", {"start": v(690, -11.88) * mm, "end": v(690, -24) * mm});
            skLineSegment(sketch, "E72.9.0.9", {"start": v(714.8, -25.2) * mm, "end": v(725.2, -25.2) * mm});
            skLineSegment(sketch, "E72.9.0.10", {"start": v(710, 14.3) * mm, "end": v(710, -14.3) * mm});
            skLineSegment(sketch, "E72.9.0.11", {"start": v(730, -14.3) * mm, "end": v(730, 14.3) * mm});
            skLineSegment(sketch, "E72.9.0.12", {"start": v(713.8, -5.4) * mm, "end": v(713.8, -24.2) * mm});
            skArc(sketch, "E72.9.0.13", {"start": v(696, 30) * mm, "mid": v(691.76, 28.24) * mm, "end": v(690, 24) * mm});
            skLineSegment(sketch, "E72.9.0.14", {"start": v(709.26, -18.26) * mm, "end": v(694, -14.17) * mm});
            skArc(sketch, "E72.9.0.15", {"start": v(750, 24) * mm, "mid": v(748.24, 28.24) * mm, "end": v(744, 30) * mm});
            skArc(sketch, "E72.9.0.16", {"start": v(744, -30) * mm, "mid": v(748.24, -28.24) * mm, "end": v(750, -24) * mm});
            skLineSegment(sketch, "E72.9.0.17", {"start": v(713.8, 24.2) * mm, "end": v(713.8, 5.4) * mm});
            skLineSegment(sketch, "E72.9.0.18", {"start": v(744, 30) * mm, "end": v(696, 30) * mm});
            skLineSegment(sketch, "E72.9.0.19", {"start": v(696, -27.25) * mm, "end": v(709, -27.25) * mm});
            skLineSegment(sketch, "E72.9.0.20", {"start": v(694, 14.17) * mm, "end": v(709.26, 18.26) * mm});
            skLineSegment(sketch, "E72.9.0.21", {"start": v(690, 24) * mm, "end": v(690, 11.88) * mm});
            skLineSegment(sketch, "E72.9.0.22", {"start": v(725.2, 25.2) * mm, "end": v(714.8, 25.2) * mm});
            skLineSegment(sketch, "E72.9.0.23", {"start": v(731.26, 15.27) * mm, "end": v(748.43, 10.67) * mm});
            skLineSegment(sketch, "E72.9.0.24", {"start": v(692.75, 24) * mm, "end": v(692.75, 15.14) * mm});
            skLineSegment(sketch, "E72.9.0.25", {"start": v(747.25, -24) * mm, "end": v(747.25, -15.14) * mm});
            skArc(sketch, "E72.9.0.26", {"start": v(713.6, 4.8) * mm, "mid": v(712, 0) * mm, "end": v(713.6, -4.8) * mm});
            skLineSegment(sketch, "E72.9.0.27", {"start": v(692.75, -15.14) * mm, "end": v(692.75, -24) * mm});
            skLineSegment(sketch, "E72.9.0.28", {"start": v(746, -14.17) * mm, "end": v(730.74, -18.26) * mm});
            skLineSegment(sketch, "E72.9.0.29", {"start": v(708.74, -15.27) * mm, "end": v(691.57, -10.67) * mm});
            skLineSegment(sketch, "E72.9.0.30", {"start": v(750, 11.88) * mm, "end": v(750, 24) * mm});
            skLineSegment(sketch, "E72.9.0.31", {"start": v(744, 27.25) * mm, "end": v(731, 27.25) * mm});
            skArc(sketch, "E72.9.0.32", {"start": v(726.4, -4.8) * mm, "mid": v(728, 0) * mm, "end": v(726.4, 4.8) * mm});
            skArc(sketch, "E72.9.0.33", {"start": v(690, -24) * mm, "mid": v(691.76, -28.24) * mm, "end": v(696, -30) * mm});
            skLineSegment(sketch, "E72.9.0.34", {"start": v(750, -24) * mm, "end": v(750, -11.88) * mm});
            skLineSegment(sketch, "E72.9.0.35", {"start": v(709, 27.25) * mm, "end": v(696, 27.25) * mm});
            skArc(sketch, "E72.9.0.36", {"start": v(725.2, -25.2) * mm, "mid": v(725.9, -24.9) * mm, "end": v(726.2, -24.2) * mm});
            skArc(sketch, "E72.9.0.37", {"start": v(692.75, -24) * mm, "mid": v(693.7, -26.3) * mm, "end": v(696, -27.25) * mm});
            skArc(sketch, "E72.9.0.38", {"start": v(747.25, -15.14) * mm, "mid": v(746.86, -14.34) * mm, "end": v(746, -14.17) * mm});
            skArc(sketch, "E72.9.0.39", {"start": v(730, -26.25) * mm, "mid": v(730.3, -26.96) * mm, "end": v(731, -27.25) * mm});
            skArc(sketch, "E72.9.0.40", {"start": v(726.2, 5.4) * mm, "mid": v(726.25, 5.08) * mm, "end": v(726.4, 4.8) * mm});
            skArc(sketch, "E72.9.0.41", {"start": v(744, -27.25) * mm, "mid": v(746.3, -26.3) * mm, "end": v(747.25, -24) * mm});
            skArc(sketch, "E72.9.0.42", {"start": v(713.6, 4.8) * mm, "mid": v(713.75, 5.08) * mm, "end": v(713.8, 5.4) * mm});
            skLineSegment(sketch, "E72.9.0.43", {"start": v(730, 26.25) * mm, "end": v(730, 19.22) * mm});
            skArc(sketch, "E72.9.0.44", {"start": v(750, -11.88) * mm, "mid": v(749.51, -10.89) * mm, "end": v(748.43, -10.67) * mm});
            skArc(sketch, "E72.9.0.45", {"start": v(730, -14.3) * mm, "mid": v(730.4, -15.1) * mm, "end": v(731.26, -15.27) * mm});
            skArc(sketch, "E72.9.0.46", {"start": v(731, 27.25) * mm, "mid": v(730.3, 26.96) * mm, "end": v(730, 26.25) * mm});
            skArc(sketch, "E72.9.0.47", {"start": v(696, 27.25) * mm, "mid": v(693.7, 26.3) * mm, "end": v(692.75, 24) * mm});
            skArc(sketch, "E72.9.0.48", {"start": v(746, 14.17) * mm, "mid": v(746.86, 14.34) * mm, "end": v(747.25, 15.14) * mm});
            skArc(sketch, "E72.9.0.49", {"start": v(748.43, 10.67) * mm, "mid": v(749.51, 10.89) * mm, "end": v(750, 11.88) * mm});
            skArc(sketch, "E72.9.0.50", {"start": v(730, 19.22) * mm, "mid": v(730.2, 18.61) * mm, "end": v(730.74, 18.26) * mm});
            skArc(sketch, "E72.9.0.51", {"start": v(731.26, 15.27) * mm, "mid": v(730.4, 15.1) * mm, "end": v(730, 14.3) * mm});
            skArc(sketch, "E72.9.0.52", {"start": v(747.25, 24) * mm, "mid": v(746.3, 26.3) * mm, "end": v(744, 27.25) * mm});
            skArc(sketch, "E72.9.0.53", {"start": v(691.57, -10.67) * mm, "mid": v(690.49, -10.89) * mm, "end": v(690, -11.88) * mm});
            skLineSegment(sketch, "E72.9.0.54", {"start": v(730, -19.22) * mm, "end": v(730, -26.25) * mm});
            skArc(sketch, "E72.9.0.55", {"start": v(713.8, -24.2) * mm, "mid": v(714.1, -24.9) * mm, "end": v(714.8, -25.2) * mm});
            skArc(sketch, "E72.9.0.56", {"start": v(730.74, -18.26) * mm, "mid": v(730.2, -18.61) * mm, "end": v(730, -19.22) * mm});
            skArc(sketch, "E72.9.0.57", {"start": v(694, -14.17) * mm, "mid": v(693.14, -14.34) * mm, "end": v(692.75, -15.14) * mm});
            skArc(sketch, "E72.9.0.58", {"start": v(690, 11.88) * mm, "mid": v(690.49, 10.89) * mm, "end": v(691.57, 10.67) * mm});
            skLineSegment(sketch, "E72.9.0.59", {"start": v(710, -26.25) * mm, "end": v(710, -19.22) * mm});
            skArc(sketch, "E72.9.0.60", {"start": v(709.26, 18.26) * mm, "mid": v(709.8, 18.61) * mm, "end": v(710, 19.22) * mm});
            skArc(sketch, "E72.9.0.61", {"start": v(726.2, 24.2) * mm, "mid": v(725.9, 24.9) * mm, "end": v(725.2, 25.2) * mm});
            skArc(sketch, "E72.9.0.62", {"start": v(692.75, 15.14) * mm, "mid": v(693.14, 14.34) * mm, "end": v(694, 14.17) * mm});
            skArc(sketch, "E72.9.0.63", {"start": v(710, -19.22) * mm, "mid": v(709.8, -18.61) * mm, "end": v(709.26, -18.26) * mm});
            skArc(sketch, "E72.9.0.64", {"start": v(714.8, 25.2) * mm, "mid": v(714.1, 24.9) * mm, "end": v(713.8, 24.2) * mm});
            skArc(sketch, "E72.9.0.65", {"start": v(710, 26.25) * mm, "mid": v(709.7, 26.96) * mm, "end": v(709, 27.25) * mm});
            skArc(sketch, "E72.9.0.66", {"start": v(710, 14.3) * mm, "mid": v(709.6, 15.1) * mm, "end": v(708.74, 15.27) * mm});
            skLineSegment(sketch, "E72.9.0.67", {"start": v(710, 19.22) * mm, "end": v(710, 26.25) * mm});
            skArc(sketch, "E72.9.0.68", {"start": v(708.74, -15.27) * mm, "mid": v(709.6, -15.1) * mm, "end": v(710, -14.3) * mm});
            skArc(sketch, "E72.9.0.69", {"start": v(709, -27.25) * mm, "mid": v(709.7, -26.96) * mm, "end": v(710, -26.25) * mm});
            skArc(sketch, "E72.9.0.70", {"start": v(726.4, -4.8) * mm, "mid": v(726.25, -5.08) * mm, "end": v(726.2, -5.4) * mm});
            skArc(sketch, "E72.9.0.71", {"start": v(713.8, -5.4) * mm, "mid": v(713.75, -5.08) * mm, "end": v(713.6, -4.8) * mm});
            skLineSegment(sketch, "E72.direction1", {"start": v(-24, -30) * mm, "end": v(56, -30) * mm, "construction": true});
            skSolve(sketch);
        }
        {
            var Q0;
            Q0=makeQuery(id+"F0.imprint","IMPRINT",FACE,{"disambiguationData":[TD([[makeQuery(id+"F0.imprint","IMPRINT",EDGE,{"derivedFrom":sQuery(id+"F0.wireOp",EDGE,"E0")}),-1.0]])]});
            extrude(context, id + "F1", {"entities" : qUnion([Q0]), "depth" : 1000 * mm, "offsetDistance" : 25 * mm});
        }
        {
            var Q0;
            Q0=makeQuery(id+"F0.imprint","IMPRINT",FACE,{"disambiguationData":[TD([[makeQuery(id+"F0.imprint","IMPRINT",EDGE,{"derivedFrom":sQuery(id+"F0.wireOp",EDGE,"E72.1.0.0")}),-1.0]])]});
            extrude(context, id + "F2", {"entities" : qUnion([Q0]), "depth" : 1600 * mm, "offsetDistance" : 25 * mm});
        }
    });
